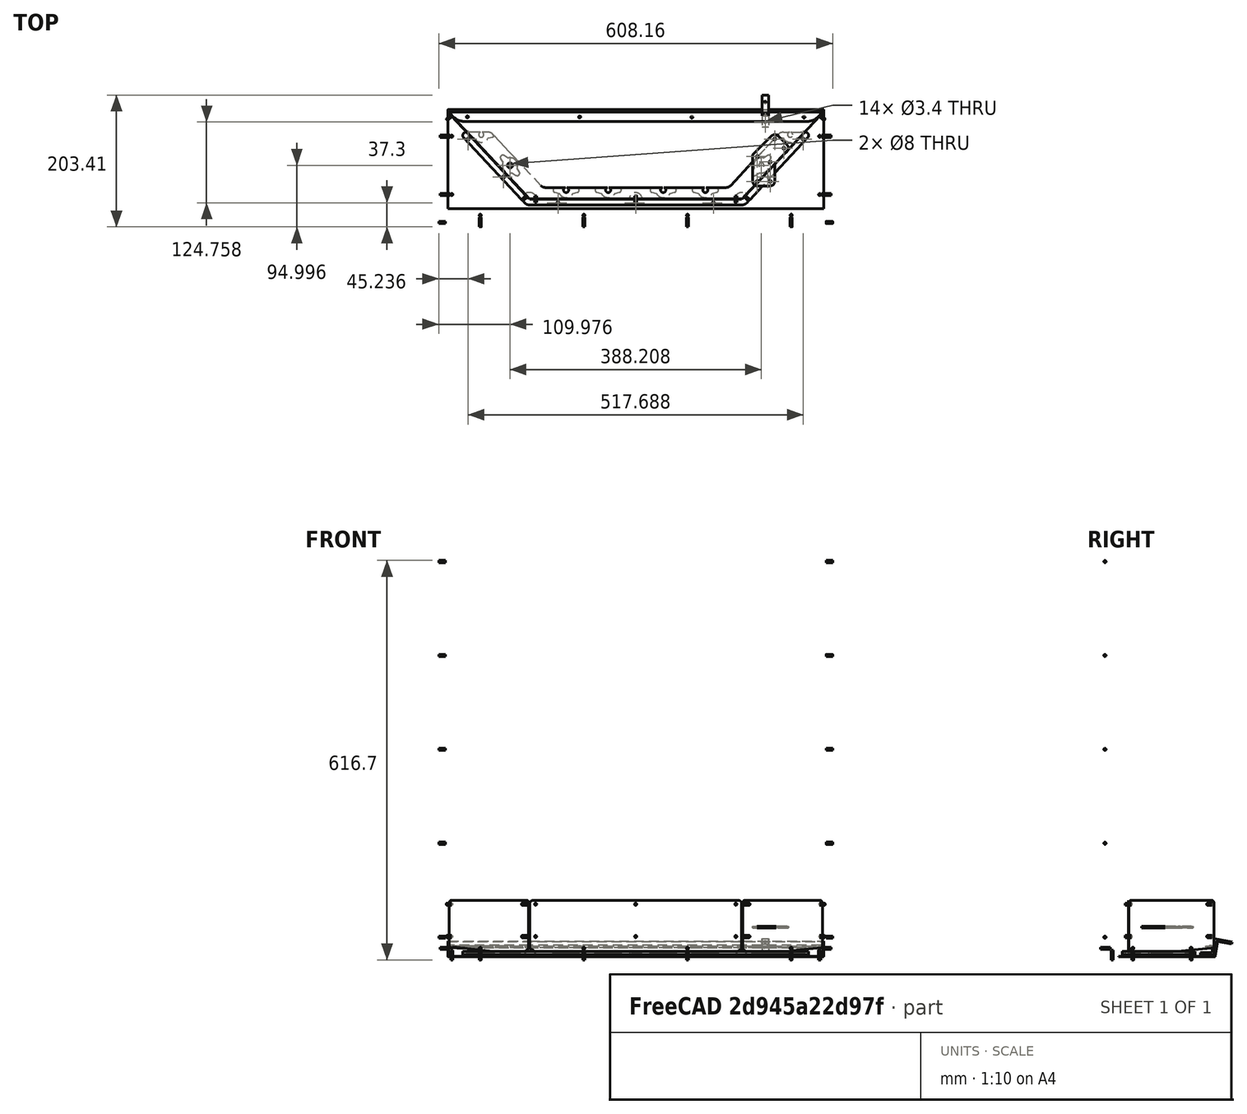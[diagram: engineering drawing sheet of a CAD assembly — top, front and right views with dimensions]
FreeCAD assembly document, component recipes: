
FREECAD ASSEMBLY — COMPONENT RECIPES ("composit_stand5")

This assembly document has 19 components, labeled P0..P18 below (a component is one placed body or linked part). 18 of them carry a construction recipe — the FreeCAD feature program that regenerates the part from scratch, quoted from this document or its linked companion documents; the rest are supplied as boundary geometry only. No exploded tour is included for this assembly.
NOTE — this tour is split across 2 documents so each fits a 32k-token context. This is document 1: the component sections continue in the remaining 1 document, each repeating the header above.
COMPONENT P0 — recipe-attached ("back_material_0.30ansi", modeled in this document).
Construction recipe (the document's own serialized feature program — sketch geometry with constraints, then the solid features built on it; lengths are millimeters unless a unit is written):

FEATURE [PartDesign::SubShapeBinder] Binder011
  BindCopyOnChange = 0
  BindMode = 0
  ClaimChildren = true
  Context = -> Body004 [Binder011.]
  Fuse = false
  MakeFace = true
  OffsetFill = false
  OffsetIntersection = false
  OffsetJoinType = 0
  OffsetOpenResult = false
  PartialLoad = false
  Relative = true
  Support = -> [Body[BaseBend.Sketch.]]
  _Version = 2
FEATURE [Sketcher::SketchObject] Sketch012
  ExternalGeometry = -> [Binder011]
  FullyConstrained = true
  MapMode = 5
  Support = -> [XY_Plane004]
  sketch-geometry (3):
    g0: LineSegment StartX=297.084 StartY=-31 StartZ=0 EndX=297.084 EndY=-41 EndZ=0
    g1: LineSegment StartX=297.084 StartY=-41 StartZ=0 EndX=-297.084 EndY=-41 EndZ=0
    g2: LineSegment StartX=-297.084 StartY=-41 StartZ=0 EndX=-297.084 EndY=-31 EndZ=0
  constraints (9):
    c: Vertical(g0)
    c: Coincident(g0,g1)
    c: Horizontal(g1)
    c: Coincident(g1,g2)
    c: Vertical(g2)
    c: Symmetric(g2,g0,g-2)
    c: DistanceY(g0,g0) = 10
    c: Horizontal(g0,g-3)
    c: DistanceX(g0,g-3) = 3
FEATURE [PartDesign::FeaturePython] BaseBend003  # WARN: FeaturePython — macro-defined, semantics opaque (R4)
  BendSide = 0
  BendSketch = -> Sketch012
  MidPlane = false
  Reverse = false
  length = 637
  radius = 0.1
  thickness = 0.3
  expr: length = BaseBend.length - 3 mm
FEATURE [PartDesign::FeaturePython] Extend  # WARN: FeaturePython — macro-defined, semantics opaque (R4)
  BaseFeature = -> BaseBend003
  Offset = 0.02
  Refine = true
  UseSubtraction = false
  baseObject = -> BaseBend003 [Face12]
  gap1 = 0
  gap2 = 0
  length = 50.4
  expr: length = <<cap_BaseBend>>.length + 0.4 mm
FEATURE [PartDesign::FeaturePython] Extend001  # WARN: FeaturePython — macro-defined, semantics opaque (R4)
  BaseFeature = -> Extend
  Offset = 0.02
  Refine = true
  UseSubtraction = false
  baseObject = -> Extend [Face12]
  gap1 = 0
  gap2 = 0
  length = 6
FEATURE [PartDesign::Boolean] Boolean002
  BaseFeature = -> Extend001
  Group = -> [Compound007]
  Type = 1
  expr: Group = <<back_cut1>>._self
FEATURE [PartDesign::Body] Body004  label="back_material_0.30ansi"
  Group = -> [Binder011,Sketch012,BaseBend003,Extend,Extend001,Boolean002]
  Origin = -> Origin004
  Tip = -> Extend001
COMPONENT P1 — recipe-attached ("Body008_material_0.30ansi", modeled in this document).
Construction recipe (the document's own serialized feature program — sketch geometry with constraints, then the solid features built on it; lengths are millimeters unless a unit is written):

FEATURE [Sketcher::SketchObject] Sketch021
  FullyConstrained = true
  MapMode = 5
  Placement = pos=(0,0,0) rot=(0.57735,0.57735,0.57735;2.0944rad)
  Support = -> [YZ_Plane009]
  sketch-geometry (5):
    g0: LineSegment StartX=27 StartY=0 StartZ=0 EndX=15 EndY=0 EndZ=0
    g1: LineSegment StartX=15 StartY=0 StartZ=0 EndX=15 EndY=16 EndZ=0
    g2: LineSegment StartX=15 StartY=16 StartZ=0 EndX=-15 EndY=16 EndZ=0
    g3: LineSegment StartX=-15 StartY=16 StartZ=0 EndX=-15 EndY=0 EndZ=0
    g4: LineSegment StartX=-15 StartY=0 StartZ=0 EndX=-27 EndY=0 EndZ=0
  constraints (15):
    c: PointOnObject(g0,g-1)
    c: PointOnObject(g0,g-1)
    c: Coincident(g0,g1)
    c: Vertical(g1)
    c: Coincident(g1,g2)
    c: PointOnObject(g3,g-1)
    c: Vertical(g3)
    c: Coincident(g3,g4)
    c: PointOnObject(g4,g-1)
    c: Symmetric(g2,g1,g-2)
    c: Coincident(g3,g2)
    c: DistanceX(g2,g2) = 30
    c: DistanceY(g1,g1) = 16  'height'
    c: Equal(g0,g4)
    c: DistanceX(g0,g0) = 12
FEATURE [PartDesign::FeaturePython] BaseBend005  # WARN: FeaturePython — macro-defined, semantics opaque (R4)
  BendSide = 0
  BendSketch = -> Sketch021
  MidPlane = true
  Reverse = false
  length = 115
  radius = 0.1
  thickness = 0.3
FEATURE [PartDesign::FeaturePython] Bend004  # WARN: FeaturePython — macro-defined, semantics opaque (R4)
  AutoMiter = true
  BaseFeature = -> BaseBend005
  BendType = 0
  LengthList = [16]
  LengthSpec = 1
  ReliefFactor = 0.7
  UseReliefFactor = false
  angle = 90
  baseObject = -> BaseBend005 [Edge45,Edge42]
  bendAList = [90]
  extend1 = 0
  extend2 = 0
  gap1 = 0
  gap2 = 0
  invert = false
  kfactor = 0.5
  length = 16
  maxExtendDist = 5
  minGap = 0.1
  minReliefGap = 1
  miterangle1 = 0
  miterangle2 = 0
  offset = 0
  radius = 0.1
  reliefType = 0
  reliefd = 1
  reliefw = 0.8
  sketchflip = false
  sketchinvert = false
  unfold = false
  expr: baseObject = tuple(BaseBend005._self; list(<<Edge45>>; <<Edge42>>))
  expr: length = Sketch021.Constraints.height
  expr: radius = BaseBend005.radius
FEATURE [Sketcher::SketchObject] Sketch022
  ExternalGeometry = -> [Sketch021]
  FullyConstrained = true
  MapMode = 5
  Support = -> [XY_Plane009]
  sketch-geometry (10):
    g0: LineSegment StartX=-35 StartY=-20.7 StartZ=0 EndX=-35 EndY=20.7 EndZ=0
    g1: LineSegment StartX=-35 StartY=20.7 StartZ=0 EndX=35 EndY=20.7 EndZ=0
    g2: LineSegment StartX=35 StartY=20.7 StartZ=0 EndX=35 EndY=-20.7 EndZ=0
    g3: LineSegment StartX=35 StartY=-20.7 StartZ=0 EndX=-35 EndY=-20.7 EndZ=0
    g4: GeomPoint X=0 Y=0 Z=0
    g5: Circle CenterX=35 CenterY=20.7 CenterZ=0 NormalX=0 NormalY=0 NormalZ=1 AngleXU=0 Radius=1.7
    g6: Circle CenterX=35 CenterY=-20.7 CenterZ=0 NormalX=0 NormalY=0 NormalZ=1 AngleXU=0 Radius=1.7
    g7: Circle CenterX=-35 CenterY=-20.7 CenterZ=0 NormalX=0 NormalY=0 NormalZ=1 AngleXU=0 Radius=1.7
    g8: Circle CenterX=-35 CenterY=20.7 CenterZ=0 NormalX=0 NormalY=0 NormalZ=1 AngleXU=0 Radius=1.7
    g9: GeomPoint X=35 Y=19 Z=0
  constraints (22):
    c: Coincident(g0,g1)
    c: Coincident(g1,g2)
    c: Coincident(g2,g3)
    c: Coincident(g3,g0)
    c: Horizontal(g1)
    c: Horizontal(g3)
    c: Vertical(g0)
    c: Vertical(g2)
    c: Symmetric(g1,g0,g4)
    c: Coincident(g4,g-1)
    c: Coincident(g6,g2)
    c: Coincident(g7,g0)
    c: Coincident(g8,g0)
    c: Coincident(g5,g1)
    c: Equal(g5,g8)
    c: Equal(g5,g7)
    c: Equal(g5,g6)
    c: Diameter(g5) = 3.4
    c: PointOnObject(g9,g2)
    c: PointOnObject(g9,g5)
    c: DistanceY(g-3,g9) = 4
    c: DistanceX(g1,g1) = 70
FEATURE [PartDesign::Pocket] Pocket016
  BaseFeature = -> Bend004
  Direction = (0,0,-1)
  Length = 5
  Length2 = 5
  Profile = -> Sketch022
  ReferenceAxis = -> Sketch022 [N_Axis]
  Reversed = true
  Type = 0
FEATURE [Sketcher::SketchObject] Sketch023
  AttachmentOffset = pos=(0,10,15) rot=(0,0,1;0rad)
  FullyConstrained = false
  MapMode = 5
  Placement = pos=(0,-15,10) rot=(1,0,0;1.5708rad)
  Support = -> [XZ_Plane009]
  sketch-geometry (8):
    g0: ArcOfCircle CenterX=47.5 CenterY=0 CenterZ=0 NormalX=0 NormalY=0 NormalZ=1 AngleXU=0 Radius=2.75 StartAngle=1.5708 EndAngle=4.71239
    g1: ArcOfCircle CenterX=86.6111 CenterY=0 CenterZ=0 NormalX=0 NormalY=0 NormalZ=1 AngleXU=0 Radius=2.75 StartAngle=4.71239 EndAngle=7.85398
    g2: LineSegment StartX=47.5 StartY=-2.75 StartZ=0 EndX=86.6111 EndY=-2.75 EndZ=0
    g3: LineSegment StartX=86.6111 StartY=2.75 StartZ=0 EndX=47.5 EndY=2.75 EndZ=0
    g4: ArcOfCircle CenterX=-47.5 CenterY=0 CenterZ=0 NormalX=0 NormalY=0 NormalZ=1 AngleXU=0 Radius=2.75 StartAngle=4.71239 EndAngle=7.85398
    g5: ArcOfCircle CenterX=-86.6111 CenterY=0 CenterZ=0 NormalX=0 NormalY=0 NormalZ=1 AngleXU=0 Radius=2.75 StartAngle=1.5708 EndAngle=4.71239
    g6: LineSegment StartX=-47.5 StartY=2.75 StartZ=0 EndX=-86.6111 EndY=2.75 EndZ=0
    g7: LineSegment StartX=-86.6111 StartY=-2.75 StartZ=0 EndX=-47.5 EndY=-2.75 EndZ=0
  constraints (17):
    c: Tangent(g0,g2) = -1.5708
    c: Tangent(g2,g1) = -1.5708
    c: Tangent(g1,g3) = -1.5708
    c: Tangent(g3,g0) = -1.5708
    c: Equal(g0,g1)
    c: PointOnObject(g0,g-1)
    c: PointOnObject(g1,g-1)
    c: Tangent(g4,g6) = -1.5708
    c: Tangent(g6,g5) = -1.5708
    c: Tangent(g5,g7) = -1.5708
    c: Tangent(g7,g4) = -1.5708
    c: Equal(g4,g5)
    c: Equal(g4,g0)
    c: Symmetric(g4,g0,g-2)
    c: Symmetric(g5,g1,g-2)
    c: Diameter(g0) = 5.5
    c: DistanceX(g4,g0) = 95
FEATURE [PartDesign::Pocket] Pocket018
  BaseFeature = -> Pocket016
  Direction = (0,1,-2e-16)
  Length = 5
  Length2 = 5
  Profile = -> Sketch023
  ReferenceAxis = -> Sketch023 [N_Axis]
  Reversed = true
  Type = 0
FEATURE [PartDesign::Body] Body008  label="Body008_material_0.30ansi"
  Group = -> [Sketch021,BaseBend005,Bend004,Sketch022,Pocket016,Sketch023,Pocket018]
  Origin = -> Origin009
  Tip = -> Pocket018
COMPONENT P2 — recipe-attached ("Body010", modeled in this document).
Construction recipe (the document's own serialized feature program — sketch geometry with constraints, then the solid features built on it; lengths are millimeters unless a unit is written):

FEATURE [PartDesign::FeatureBase] BaseFeature
  BaseFeature = -> Unfold
  Placement = pos=(0,0,0) rot=(1,0,0;1.5708rad)
  expr: Placement = .BaseFeature.Placement
FEATURE [PartDesign::SubShapeBinder] Binder020
  BindCopyOnChange = 0
  BindMode = 0
  ClaimChildren = false
  Context = -> Body010 [Binder020.]
  Fuse = false
  MakeFace = true
  OffsetFill = false
  OffsetIntersection = false
  OffsetJoinType = 0
  OffsetOpenResult = false
  PartialLoad = false
  Relative = true
  Support = -> [Unfold_Sketch_bends]
  _Version = 2
FEATURE [Sketcher::SketchObject] Sketch032
  ExternalGeometry = -> [Binder020]
  FullyConstrained = true
  MapMode = 5
  Support = -> [XY_Plane012]
  sketch-geometry (3):
    g0: Circle CenterX=154.334 CenterY=-0.975351 CenterZ=0 NormalX=0 NormalY=0 NormalZ=1 AngleXU=0 Radius=1
    g1: Circle CenterX=171.087 CenterY=6.35397 CenterZ=0 NormalX=0 NormalY=0 NormalZ=1 AngleXU=0 Radius=1
    g2: Circle CenterX=287.707 CenterY=131.643 CenterZ=0 NormalX=0 NormalY=0 NormalZ=1 AngleXU=0 Radius=1
  constraints (6):
    c: Coincident(g0,g-4)
    c: Coincident(g1,g-3)
    c: Coincident(g2,g-3)
    c: Equal(g0,g1)
    c: Equal(g0,g2)
    c: Diameter(g0) = 2
FEATURE [PartDesign::Pocket] Pocket023
  BaseFeature = -> BaseFeature
  Direction = (0,0,-1)
  Length = 5
  Length2 = 5
  Placement = pos=(0,0,0) rot=(1,0,0;1.5708rad)
  Profile = -> Sketch032
  ReferenceAxis = -> Sketch032 [N_Axis]
  Reversed = true
  Type = 0
FEATURE [PartDesign::Mirrored] Mirrored006
  BaseFeature = -> Pocket023
  MirrorPlane = -> Sketch032 [V_Axis]
  Originals = -> [Pocket023]
  Placement = pos=(0,0,0) rot=(1,0,0;1.5708rad)
FEATURE [PartDesign::Body] Body010
  BaseFeature = -> Unfold
  Group = -> [BaseFeature,Sketch032,Binder020,Pocket023,Mirrored006]
  Origin = -> Origin012
  Tip = -> Mirrored006
COMPONENT P3 — recipe-attached ("front_shield", modeled in this document).
Construction recipe (the document's own serialized feature program — sketch geometry with constraints, then the solid features built on it; lengths are millimeters unless a unit is written):

FEATURE [PartDesign::SubShapeBinder] Binder028
  BindCopyOnChange = 0
  BindMode = 0
  ClaimChildren = false
  Context = -> Body015 [Binder028.]
  Fuse = false
  MakeFace = true
  OffsetFill = false
  OffsetIntersection = false
  OffsetJoinType = 0
  OffsetOpenResult = false
  PartialLoad = false
  Relative = true
  Support = -> [Body[Sketch046.]]
  _Version = 2
FEATURE [Sketcher::SketchObject] Sketch057
  ExternalGeometry = -> [Binder028]
  FullyConstrained = true
  MapMode = 5
  Support = -> [XY_Plane018]
  sketch-geometry (2):
    g0: LineSegment StartX=281.847 StartY=125.257 StartZ=0 EndX=287.276 EndY=131.058 EndZ=0
    g1: LineSegment StartX=281.847 StartY=125.257 StartZ=0 EndX=-281.847 EndY=125.257 EndZ=0
  constraints (6):
    c: Parallel(g-3,g0)
    c: Distance(g-4,g0) = 3
    c: Coincident(g1,g0)
    c: Distance(g-4,g1) = 4.5
    c: Symmetric(g1,g1,g-2)
    c: Horizontal(g0,g-3)
FEATURE [PartDesign::FeaturePython] BaseBend009  # WARN: FeaturePython — macro-defined, semantics opaque (R4)
  BendSide = 0
  BendSketch = -> Sketch057
  MidPlane = false
  Reverse = false
  length = 115
  radius = 1
  thickness = 1
FEATURE [PartDesign::SubShapeBinder] Binder030
  BindCopyOnChange = 0
  BindMode = 0
  ClaimChildren = false
  Context = -> Body015 [Binder030.]
  Fuse = false
  MakeFace = true
  OffsetFill = false
  OffsetIntersection = false
  OffsetJoinType = 0
  OffsetOpenResult = false
  PartialLoad = false
  Relative = true
  _Version = 2
FEATURE [Sketcher::SketchObject] Sketch077
  FullyConstrained = true
  MapMode = 5
  Placement = pos=(0,0,0) rot=(1,0,0;1.5708rad)
  Support = -> [XZ_Plane018]
  sketch-geometry (1):
    g0: Circle CenterX=242 CenterY=85 CenterZ=0 NormalX=0 NormalY=0 NormalZ=1 AngleXU=0 Radius=15
  constraints (3):
    c: Diameter(g0) = 30
    c: DistanceX(g0) = 242
    c: DistanceY(g0) = 85
FEATURE [PartDesign::Pocket] Pocket052
  BaseFeature = -> BaseBend009
  Direction = (0,1,-2e-16)
  Length = 5
  Length2 = 5
  Midplane = true
  Profile = -> Sketch077
  ReferenceAxis = -> Sketch077 [N_Axis]
  Type = 1
FEATURE [Sketcher::SketchObject] Sketch078
  FullyConstrained = true
  MapMode = 5
  Placement = pos=(0,0,0) rot=(1,0,0;1.5708rad)
  Support = -> [XZ_Plane018]
  sketch-geometry (2):
    g0: Circle CenterX=271 CenterY=75 CenterZ=0 NormalX=0 NormalY=0 NormalZ=1 AngleXU=0 Radius=1.7
    g1: Circle CenterX=271 CenterY=35 CenterZ=0 NormalX=0 NormalY=0 NormalZ=1 AngleXU=0 Radius=1.7
  constraints (6):
    c: Vertical(g1,g0)
    c: DistanceY(g1,g0) = 40
    c: DistanceX(g0) = 271
    c: DistanceY(g0) = 75
    c: Equal(g1,g0)
    c: Diameter(g1) = 3.4
FEATURE [PartDesign::Pocket] Pocket
  BaseFeature = -> Pocket052
  Direction = (0,1,-2e-16)
  Length = 5
  Length2 = 5
  Midplane = true
  Profile = -> Sketch078
  ReferenceAxis = -> Sketch078 [N_Axis]
  Type = 1
FEATURE [PartDesign::Mirrored] Mirrored012
  BaseFeature = -> Pocket
  MirrorPlane = -> Sketch077 [V_Axis]
  Originals = -> [Pocket052,Pocket]
FEATURE [PartDesign::Body] Body015  label="front_shield"
  Group = -> [Sketch057,Binder028,BaseBend009,Binder030,Sketch077,Pocket052,Sketch078,Pocket,Mirrored012]
  Origin = -> Origin018
  Tip = -> Mirrored012
COMPONENT P4 — recipe-attached ("Body016_material_0.30ansi", modeled in this document).
Construction recipe (the document's own serialized feature program — sketch geometry with constraints, then the solid features built on it; lengths are millimeters unless a unit is written):

FEATURE [PartDesign::SubShapeBinder] Binder029
  BindCopyOnChange = 0
  BindMode = 0
  ClaimChildren = false
  Context = -> Body016 [Binder029.]
  Fuse = false
  MakeFace = true
  OffsetFill = false
  OffsetIntersection = false
  OffsetJoinType = 0
  OffsetOpenResult = false
  PartialLoad = false
  Relative = true
  Support = -> [Body[BaseBend.Sketch.]]
  _Version = 2
FEATURE [Sketcher::SketchObject] Sketch058
  ExternalGeometry = -> [Binder029]
  FullyConstrained = true
  MapMode = 5
  Support = -> [XY_Plane019]
  sketch-geometry (9):
    g0: LineSegment StartX=-297.084 StartY=131.058 StartZ=0 EndX=-297.084 EndY=-38 EndZ=0
    g1: LineSegment StartX=-297.084 StartY=-38 StartZ=0 EndX=297.084 EndY=-38 EndZ=0
    g2: LineSegment StartX=297.084 StartY=-38 StartZ=0 EndX=297.084 EndY=131.058 EndZ=0
    g3: LineSegment StartX=297.084 StartY=131.058 StartZ=0 EndX=-297.084 EndY=131.058 EndZ=0
    g4: GeomPoint X=0 Y=46.5289 Z=0
    g5: LineSegment StartX=297.084 StartY=134.058 StartZ=0 EndX=297.084 EndY=131.058 EndZ=0
    g6: LineSegment StartX=297.084 StartY=131.058 StartZ=0 EndX=300.084 EndY=131.058 EndZ=0
    g7: LineSegment StartX=297.084 StartY=-41 StartZ=0 EndX=297.084 EndY=-38 EndZ=0
    g8: LineSegment StartX=297.084 StartY=-38 StartZ=0 EndX=300.084 EndY=-38 EndZ=0
  constraints (25):
    c: Coincident(g0,g1)
    c: Coincident(g1,g2)
    c: Coincident(g2,g3)
    c: Coincident(g3,g0)
    c: Horizontal(g1)
    c: Horizontal(g3)
    c: Vertical(g0)
    c: Vertical(g2)
    c: Symmetric(g1,g0,g4)
    c: PointOnObject(g4,g-2)
    c: Coincident(g5,g2)
    c: Coincident(g5,g6)
    c: PointOnObject(g6,g-3)
    c: Coincident(g7,g1)
    c: Coincident(g7,g8)
    c: PointOnObject(g8,g-3)
    c: Horizontal(g8)
    c: Horizontal(g7,g-3)
    c: Vertical(g7)
    c: Equal(g7,g8)
    c: Equal(g8,g6)
    c: Equal(g6,g5)
    c: Horizontal(g5,g-3)
    c: Parallel(g5,g2)
    c: DistanceX(g6,g6) = 3
FEATURE [PartDesign::FeaturePython] BaseBend010  # WARN: FeaturePython — macro-defined, semantics opaque (R4)
  BendSide = 0
  BendSketch = -> Sketch058
  MidPlane = false
  Reverse = true
  length = 100
  radius = 0.1
  thickness = 0.3
  expr: radius = composit_properties#<<Properties>>.bend_r
  expr: thickness = composit_properties#<<Properties>>.al_thickness
FEATURE [PartDesign::FeaturePython] Bend009  # WARN: FeaturePython — macro-defined, semantics opaque (R4)
  AutoMiter = true
  BaseFeature = -> BaseBend010
  BendType = 1
  LengthList = [3]
  LengthSpec = 1
  ReliefFactor = 0.7
  UseReliefFactor = false
  angle = 90
  baseObject = -> BaseBend010 [Edge11]
  bendAList = [90]
  extend1 = 0
  extend2 = 0
  gap1 = 0
  gap2 = 0
  invert = false
  kfactor = 0.5
  length = 3
  maxExtendDist = 5
  minGap = 0.1
  minReliefGap = 1
  miterangle1 = 0
  miterangle2 = 0
  offset = 0
  radius = 0.1
  reliefType = 0
  reliefd = 1
  reliefw = 0.8
  sketchflip = false
  sketchinvert = false
  unfold = false
  expr: length = composit_properties#<<Properties>>.thickness
  expr: radius = BaseBend005.radius
FEATURE [Sketcher::SketchObject] Sketch059
  ExternalGeometry = -> [Sketch058]
  FullyConstrained = true
  MapMode = 5
  Support = -> [XY_Plane019]
  sketch-geometry (7):
    g0: LineSegment StartX=0 StartY=131.058 StartZ=0 EndX=0 EndY=121.058 EndZ=0
    g1: LineSegment StartX=0 StartY=-28 StartZ=0 EndX=0 EndY=-38 EndZ=0
    g2: Circle CenterX=0 CenterY=121.058 CenterZ=0 NormalX=0 NormalY=0 NormalZ=1 AngleXU=0 Radius=1.7
    g3: Circle CenterX=0 CenterY=-28 CenterZ=0 NormalX=0 NormalY=0 NormalZ=1 AngleXU=0 Radius=1.7
    g4: LineSegment StartX=0 StartY=121.058 StartZ=0 EndX=0 EndY=46.5289 EndZ=0
    g5: LineSegment StartX=0 StartY=46.5289 StartZ=0 EndX=0 EndY=-28 EndZ=0
    g6: Circle CenterX=0 CenterY=46.5289 CenterZ=0 NormalX=0 NormalY=0 NormalZ=1 AngleXU=0 Radius=1.7
  constraints (19):
    c: PointOnObject(g0,g-3)
    c: PointOnObject(g0,g-2)
    c: Vertical(g0)
    c: Coincident(g0,g4)
    c: PointOnObject(g5,g-2)
    c: Coincident(g5,g1)
    c: PointOnObject(g1,g-4)
    c: Vertical(g1)
    c: Coincident(g2,g0)
    c: Coincident(g3,g5)
    c: Coincident(g4,g5)
    c: Coincident(g6,g4)
    c: Equal(g5,g4)
    c: Equal(g0,g1)
    c: DistanceY(g1,g1) = 10
    c: Equal(g3,g6)
    c: Equal(g3,g2)
    c: Diameter(g3) = 3.4
    c: PointOnObject(g6,g-2)
FEATURE [PartDesign::Boolean] Boolean003
  BaseFeature = -> Bend009
  Type = 1
FEATURE [PartDesign::Body] Body016  label="Body016_material_0.30ansi"
  Group = -> [Binder029,Sketch058,BaseBend010,Bend009,Sketch059,Boolean003]
  Origin = -> Origin019
  Placement = pos=(0,0,-3) rot=(0,0,1;0rad)
  Tip = -> Boolean003
COMPONENT P5 — recipe-attached ("Body019", modeled in this document).
Construction recipe (the document's own serialized feature program — sketch geometry with constraints, then the solid features built on it; lengths are millimeters unless a unit is written):

FEATURE [PartDesign::SubShapeBinder] Binder033
  BindCopyOnChange = 0
  BindMode = 0
  ClaimChildren = false
  Context = -> Body019 [Binder033.]
  Fuse = false
  MakeFace = true
  OffsetFill = false
  OffsetIntersection = false
  OffsetJoinType = 0
  OffsetOpenResult = false
  PartialLoad = false
  Relative = true
  Support = -> [Sketch005]
  _Version = 2
FEATURE [Sketcher::SketchObject] Sketch062
  ExternalGeometry = -> [Binder033]
  FullyConstrained = true
  MapMode = 5
  Support = -> [XY_Plane022]
  sketch-geometry (9):
    g0: LineSegment StartX=280.724 StartY=124.058 StartZ=0 EndX=261.224 EndY=124.058 EndZ=0
    g1: LineSegment StartX=261.224 StartY=124.058 StartZ=0 EndX=261.224 EndY=103.223 EndZ=0
    g2: LineSegment StartX=261.224 StartY=103.223 StartZ=0 EndX=280.724 EndY=124.058 EndZ=0
    g3: LineSegment StartX=273.808 StartY=121.058 StartZ=0 EndX=264.224 EndY=121.058 EndZ=0
    g4: LineSegment StartX=264.224 StartY=121.058 StartZ=0 EndX=264.224 EndY=110.819 EndZ=0
    g5: LineSegment StartX=264.224 StartY=110.819 StartZ=0 EndX=273.808 EndY=121.058 EndZ=0
    g6: LineSegment StartX=273.808 StartY=124.058 StartZ=0 EndX=273.808 EndY=121.058 EndZ=0
    g7: LineSegment StartX=273.808 StartY=121.058 StartZ=0 EndX=275.998 EndY=119.008 EndZ=0
    g8: LineSegment StartX=264.224 StartY=110.819 StartZ=0 EndX=261.224 EndY=110.819 EndZ=0
  constraints (27):
    c: PointOnObject(g0,g-3)
    c: Horizontal(g0)
    c: Coincident(g0,g1)
    c: PointOnObject(g1,g-3)
    c: Vertical(g1)
    c: Coincident(g1,g2)
    c: Coincident(g2,g0)
    c: DistanceX(g0,g0) = 19.5
    c: DistanceY(g0,g-3) = 10
    c: Coincident(g3,g4)
    c: Coincident(g4,g5)
    c: Coincident(g5,g3)
    c: Parallel(g3,g0)
    c: Parallel(g4,g1)
    c: Parallel(g5,g2)
    c: PointOnObject(g6,g0)
    c: Coincident(g6,g3)
    c: Coincident(g6,g7)
    c: PointOnObject(g7,g2)
    c: Coincident(g4,g8)
    c: PointOnObject(g8,g1)
    c: Horizontal(g8)
    c: Vertical(g6)
    c: Perpendicular(g2,g7)
    c: Equal(g7,g6)
    c: Equal(g6,g8)
    c: DistanceX(g8,g8) = 3
FEATURE [PartDesign::Pad] Pad007
  Direction = (0,0,1)
  Length = 18
  Length2 = 10
  Profile = -> Sketch062
  ReferenceAxis = -> Sketch062 [N_Axis]
  Type = 0
FEATURE [Sketcher::SketchObject] Sketch063
  AttachmentOffset = pos=(0,0,-124.1) rot=(0,0,1;0rad)
  ExternalGeometry = -> [Sketch062]
  FullyConstrained = true
  MapMode = 5
  Placement = pos=(0,124.1,-2.76e-14) rot=(1,0,0;1.5708rad)
  Support = -> [XZ_Plane022]
  expr: Constraints[5] = Pad007.Length / 2
  sketch-geometry (3):
    g0: Circle CenterX=270.974 CenterY=9 CenterZ=0 NormalX=0 NormalY=0 NormalZ=1 AngleXU=0 Radius=1.7
    g1: LineSegment StartX=280.724 StartY=-2.75e-14 StartZ=0 EndX=270.974 EndY=9 EndZ=0
    g2: LineSegment StartX=270.974 StartY=9 StartZ=0 EndX=261.224 EndY=-2.84e-14 EndZ=0
  constraints (7):
    c: Coincident(g-3,g1)
    c: Coincident(g1,g0)
    c: Coincident(g1,g2)
    c: Coincident(g2,g-3)
    c: Equal(g2,g1)
    c: DistanceY(g-3,g0) = 9
    c: Diameter(g0) = 3.4
FEATURE [PartDesign::Hole] Hole002
  BaseFeature = -> Pad007
  CustomThreadClearance = 0
  Depth = 8
  DepthType = 0
  Diameter = 3.4
  DrillForDepth = false
  DrillPoint = 1
  DrillPointAngle = 118
  HoleCutCountersinkAngle = 90
  HoleCutCustomValues = false
  HoleCutDepth = 0
  HoleCutDiameter = 6.1
  HoleCutType = 0
  ModelThread = false
  Profile = -> Sketch063
  Reversed = true
  Tapered = false
  TaperedAngle = 90
  ThreadClass = 0
  ThreadDepth = 8
  ThreadDepthType = 0
  ThreadDirection = 0
  ThreadFit = 0
  ThreadSize = 0
  ThreadType = 0
  Threaded = false
  UseCustomThreadClearance = false
FEATURE [Sketcher::SketchObject] Sketch064
  AttachmentOffset = pos=(0,0,0) rot=(0,1,0;1.5708rad)
  FullyConstrained = true
  MapMode = 7
  Placement = pos=(271.619,114.329,0) rot=(0.852419,0.369717,0.369717;1.7298rad)
  Support = -> [Sketch062]
  sketch-geometry (2):
    g0: Circle CenterX=0.6273 CenterY=4 CenterZ=0 NormalX=0 NormalY=0 NormalZ=1 AngleXU=0 Radius=1.7
    g1: Circle CenterX=0.6273 CenterY=14 CenterZ=0 NormalX=0 NormalY=0 NormalZ=1 AngleXU=0 Radius=1.7
  constraints (6):
    c: Diameter(g0) = 3.4
    c: DistanceY(g0) = 4
    c: DistanceX(g0) = 0.6273
    c: Equal(g1,g0)
    c: Vertical(g1,g0)
    c: DistanceY(g0,g1) = 10
FEATURE [Sketcher::SketchObject] Sketch065
  ExternalGeometry = -> [Sketch062]
  FullyConstrained = true
  MapMode = 5
  Support = -> [XY_Plane022]
  sketch-geometry (4):
    g0: LineSegment StartX=261.224 StartY=106.15 StartZ=0 EndX=275.574 EndY=121.482 EndZ=0
    g1: LineSegment StartX=261.224 StartY=124.058 StartZ=0 EndX=261.224 EndY=106.15 EndZ=0
    g2: LineSegment StartX=275.574 StartY=121.482 StartZ=0 EndX=272.822 EndY=124.058 EndZ=0
    g3: LineSegment StartX=272.822 StartY=124.058 StartZ=0 EndX=261.224 EndY=124.058 EndZ=0
  constraints (12):
    c: Coincident(g0,g2)
    c: Coincident(g3,g1)
    c: Coincident(g1,g0)
    c: Vertical(g1)
    c: Vertical(g0,g-3)
    c: Parallel(g0,g-3)
    c: Distance(g0) = 21
    c: Coincident(g2,g3)
    c: Perpendicular(g0,g2)
    c: Horizontal(g2,g-3)
    c: Distance(g0,g-3) = 2
    c: Horizontal(g3)
FEATURE [PartDesign::Plane] DatumPlane001
  AttachmentOffset = pos=(0,0,9) rot=(0,0,1;0rad)
  Length = 348.425
  MapMode = 5
  Placement = pos=(0,0,9) rot=(0,0,1;0rad)
  ResizeMode = 0
  Support = -> [XY_Plane022]
  Width = 191.801
  expr: .AttachmentOffset.Base.z = Pad007.Length / 2
FEATURE [Sketcher::SketchObject] Sketch066
  AttachmentOffset = pos=(0,0,-2) rot=(0,0,1;0rad)
  ExternalGeometry = -> [Sketch064]
  FullyConstrained = true
  MapMode = 2
  Placement = pos=(270.159,115.696,3e-16) rot=(0.852419,0.369717,0.369717;1.7298rad)
  Support = -> [Sketch064]
  sketch-geometry (1):
    g0: Circle CenterX=0.6273 CenterY=4 CenterZ=0 NormalX=0 NormalY=0 NormalZ=1 AngleXU=0 Radius=4
  constraints (2):
    c: Coincident(g0,g-3)
    c: Diameter(g0) = 8
FEATURE [Sketcher::SketchObject] Sketch071
  ExternalGeometry = -> [Sketch063]
  FullyConstrained = true
  MapMode = 2
  Placement = pos=(0,124.1,-2.76e-14) rot=(1,0,0;1.5708rad)
  Support = -> [Sketch063]
  sketch-geometry (1):
    g0: Circle CenterX=270.974 CenterY=9 CenterZ=0 NormalX=0 NormalY=0 NormalZ=1 AngleXU=0 Radius=9
  constraints (2):
    c: Coincident(g0,g-3)
    c: Diameter(g0) = 18
FEATURE [Part::FeaturePython] WireFilter  # WARN: FeaturePython — macro-defined, semantics opaque (R4)
  AttacherType = Attacher::AttachEngine3D
  ClaimChildren = true
  ColorKeyCount = 8
  Colorize = true
  FaceMaker = 5
  FixNormal = false
  FollowSource = true
  InvertedFaceScale = 5
  MaxWires = 25
  Normal = (0,1,2e-16)
  OffsetFill = false
  OffsetIntersection = false
  OffsetJoin = 0
  OffsetOpenResult = false
  Scale = (1,1,1)
  SelectEdges = false
  Source = -> Sketch071
  UniformScale = 1
  UseDefault = false
  UseSelected = true
  UseSelectedEdges = false
  Version = 0.2022.02.09
  WireOrder = [1]
FEATURE [Sketcher::SketchObject] Sketch072
  AttachmentOffset = pos=(0,0,2) rot=(0,0,1;0rad)
  ExternalGeometry = -> [Sketch063]
  FullyConstrained = true
  MapMode = 2
  Placement = pos=(0,122.1,-2.71e-14) rot=(1,0,0;1.5708rad)
  Support = -> [Sketch063]
  sketch-geometry (1):
    g0: Circle CenterX=270.974 CenterY=9 CenterZ=0 NormalX=0 NormalY=0 NormalZ=1 AngleXU=0 Radius=2.5
  constraints (2):
    c: Coincident(g0,g-3)
    c: Diameter(g0) = 5
FEATURE [PartDesign::Pocket] Pocket045
  BaseFeature = -> Hole002
  Direction = (0,1,-2e-16)
  Length = 5
  Length2 = 5
  Profile = -> Sketch072
  ReferenceAxis = -> Sketch072 [N_Axis]
  Reversed = true
  Type = 0
FEATURE [Sketcher::SketchObject] Sketch073
  FullyConstrained = false
  MapMode = 2
  Placement = pos=(271.619,114.329,0) rot=(0.852419,0.369717,0.369717;1.7298rad)
  Support = -> [Sketch064]
  sketch-geometry (4):
    g0: LineSegment StartX=-6 StartY=0 StartZ=0 EndX=-24.5767 EndY=0 EndZ=0
    g1: LineSegment StartX=-24.5767 StartY=0 StartZ=0 EndX=-24.5767 EndY=27.1269 EndZ=0
    g2: LineSegment StartX=-24.5767 StartY=27.1269 StartZ=0 EndX=-6 EndY=27.1269 EndZ=0
    g3: LineSegment StartX=-6 StartY=27.1269 StartZ=0 EndX=-6 EndY=0 EndZ=0
  constraints (10):
    c: Coincident(g0,g1)
    c: Coincident(g1,g2)
    c: Coincident(g2,g3)
    c: Coincident(g3,g0)
    c: Horizontal(g0)
    c: Horizontal(g2)
    c: Vertical(g1)
    c: Vertical(g3)
    c: PointOnObject(g0,g-1)
    c: DistanceX(g0) = -6
FEATURE [PartDesign::Pocket] Pocket046
  BaseFeature = -> Pocket045
  Direction = (-0.730107,0.683333,2e-16)
  Length = 5
  Length2 = 5
  Midplane = true
  Profile = -> Sketch073
  ReferenceAxis = -> Sketch073 [N_Axis]
  Type = 1
FEATURE [PartDesign::Pocket] Pocket040
  BaseFeature = -> Pocket046
  Direction = (-0.730107,0.683333,0)
  Length = 5
  Length2 = 5
  Midplane = true
  Profile = -> Sketch064
  ReferenceAxis = -> Sketch064 [N_Axis]
  Type = 1
FEATURE [PartDesign::Pocket] Pocket041
  BaseFeature = -> Pocket040
  Direction = (-0.730107,0.683333,2e-16)
  Length = 5
  Length2 = 5
  Profile = -> Sketch066
  ReferenceAxis = -> Sketch066 [N_Axis]
  Type = 1
FEATURE [PartDesign::Mirrored] Mirrored010
  BaseFeature = -> Pocket041
  MirrorPlane = -> DatumPlane001
  Originals = -> [Pocket040,Pocket041]
FEATURE [PartDesign::Pocket] Pocket044
  BaseFeature = -> Mirrored010
  Direction = (0,-1,-2e-16)
  Length = 5
  Length2 = 5
  Profile = -> WireFilter
  Type = 1
FEATURE [PartDesign::Body] Body019
  Group = -> [Binder033,Sketch062,Pad007,Sketch063,Hole002,Sketch064,Sketch065,DatumPlane001,Sketch071,Sketch072,Pocket045,Sketch073,Pocket046,Pocket040,Pocket041,Mirrored010,Sketch066,WireFilter,Pocket044]
  Origin = -> Origin022
  Placement = pos=(0,0,50) rot=(0,0,1;0rad)
  Tip = -> Pocket044
COMPONENT P6 — recipe-attached ("electric_shield", modeled in this document).
Construction recipe (the document's own serialized feature program — sketch geometry with constraints, then the solid features built on it; lengths are millimeters unless a unit is written):

FEATURE [PartDesign::SubShapeBinder] Binder035
  BindCopyOnChange = 0
  BindMode = 0
  ClaimChildren = false
  Context = -> Body020 [Binder035.]
  Fuse = false
  MakeFace = true
  OffsetFill = false
  OffsetIntersection = false
  OffsetJoinType = 0
  OffsetOpenResult = false
  PartialLoad = false
  Relative = true
  Support = -> [Compound009]
  _Version = 2
FEATURE [PartDesign::Pad] Pad008  label="electric_shield_extrude"
  Direction = (0,0,1)
  Length = 3
  Length2 = 10
  Profile = -> Binder035
  Type = 0
FEATURE [PartDesign::Boolean] Boolean007
  BaseFeature = -> Pad008
  Type = 1
FEATURE [PartDesign::Body] Body020  label="electric_shield"
  Group = -> [Binder035,Pad008,Boolean007]
  Origin = -> Origin023
  Tip = -> Boolean007
COMPONENT P7 — recipe-attached ("Body021", modeled in this document).
Construction recipe (the document's own serialized feature program — sketch geometry with constraints, then the solid features built on it; lengths are millimeters unless a unit is written):

FEATURE [PartDesign::SubShapeBinder] Binder038
  BindCopyOnChange = 0
  BindMode = 0
  ClaimChildren = false
  Context = -> Body021 [Binder038.]
  Fuse = false
  MakeFace = true
  OffsetFill = false
  OffsetIntersection = false
  OffsetJoinType = 0
  OffsetOpenResult = false
  PartialLoad = false
  Relative = true
  Support = -> [Body016[BaseBend010.Sketch058.]]
  _Version = 2
FEATURE [PartDesign::Pad] Pad009
  Direction = (0,0,1)
  Length = 3
  Length2 = 10
  Profile = -> Binder038
  Type = 0
FEATURE [PartDesign::Boolean] Boolean004
  BaseFeature = -> Pad009
  Type = 1
FEATURE [Sketcher::SketchObject] Sketch075
  ExternalGeometry = -> [Binder038]
  FullyConstrained = true
  MapMode = 5
  Placement = pos=(0,0,0) rot=(0.57735,0.57735,0.57735;2.0944rad)
  Support = -> [YZ_Plane024]
  sketch-geometry (3):
    g0: LineSegment StartX=131.058 StartY=3 StartZ=0 EndX=129.558 EndY=3 EndZ=0
    g1: LineSegment StartX=129.558 StartY=3 StartZ=0 EndX=131.058 EndY=1.5 EndZ=0
    g2: LineSegment StartX=131.058 StartY=1.5 StartZ=0 EndX=131.058 EndY=3 EndZ=0
  constraints (9):
    c: Horizontal(g0)
    c: Coincident(g0,g1)
    c: Coincident(g1,g2)
    c: Coincident(g2,g0)
    c: Vertical(g2)
    c: Equal(g2,g0)
    c: DistanceX(g0,g0) = 1.5
    c: DistanceY(g-3,g0) = 3
    c: Vertical(g0,g-3)
FEATURE [PartDesign::Pocket] Pocket049
  BaseFeature = -> Boolean004
  Direction = (-1,0,0)
  Length = 540
  Length2 = 5
  Midplane = true
  Profile = -> Sketch075
  ReferenceAxis = -> Sketch075 [N_Axis]
  Type = 0
FEATURE [PartDesign::Body] Body021
  Group = -> [Binder038,Pad009,Boolean004,Sketch075,Pocket049]
  Origin = -> Origin024
  Placement = pos=(0,0,-3) rot=(0,0,1;0rad)
  Tip = -> Pocket049
COMPONENT P8 — recipe-attached ("electric_shield_jamb", modeled in this document).
Construction recipe (the document's own serialized feature program — sketch geometry with constraints, then the solid features built on it; lengths are millimeters unless a unit is written):

FEATURE [PartDesign::SubShapeBinder] Binder043
  BindCopyOnChange = 0
  BindMode = 0
  ClaimChildren = true
  Context = -> Body023 [Binder043.]
  Fuse = false
  MakeFace = true
  OffsetFill = false
  OffsetIntersection = false
  OffsetJoinType = 0
  OffsetOpenResult = false
  PartialLoad = false
  Relative = false
  Support = -> [Sketch068]
  _Version = 2
FEATURE [PartDesign::Pad] Pad011
  Direction = (0,0,1)
  Length = 3
  Length2 = 10
  Profile = -> Binder043
  Type = 0
FEATURE [PartDesign::Boolean] Boolean008
  BaseFeature = -> Pad011
  Refine = true
  Type = 1
FEATURE [PartDesign::Body] Body023  label="electric_shield_jamb"
  Group = -> [Binder043,Pad011,Boolean008]
  Origin = -> Origin026
  Tip = -> Boolean008
COMPONENT P9 — recipe-attached ("Body024", modeled in this document).
Construction recipe (the document's own serialized feature program — sketch geometry with constraints, then the solid features built on it; lengths are millimeters unless a unit is written):

FEATURE [PartDesign::SubShapeBinder] Binder046
  BindCopyOnChange = 0
  BindMode = 0
  ClaimChildren = false
  Context = -> Body024 [Binder046.]
  Fuse = false
  MakeFace = true
  OffsetFill = false
  OffsetIntersection = false
  OffsetJoinType = 0
  OffsetOpenResult = false
  PartialLoad = false
  Relative = true
  Support = -> [Sketch005]
  _Version = 2
FEATURE [Sketcher::SketchObject] Sketch091
  ExternalGeometry = -> [Binder046]
  FullyConstrained = true
  MapMode = 5
  Support = -> [XY_Plane027]
  sketch-geometry (5):
    g0: LineSegment StartX=257.917 StartY=124.058 StartZ=0 EndX=277.917 EndY=124.058 EndZ=0
    g1: LineSegment StartX=277.917 StartY=124.058 StartZ=0 EndX=277.917 EndY=121.058 EndZ=0
    g2: LineSegment StartX=277.917 StartY=121.058 StartZ=0 EndX=268.578 EndY=111.08 EndZ=0
    g3: LineSegment StartX=268.578 StartY=111.08 StartZ=0 EndX=257.917 EndY=121.058 EndZ=0
    g4: LineSegment StartX=257.917 StartY=121.058 StartZ=0 EndX=257.917 EndY=124.058 EndZ=0
  constraints (16):
    c: Horizontal(g0)
    c: Coincident(g0,g1)
    c: PointOnObject(g1,g-3)
    c: Vertical(g1)
    c: Coincident(g1,g2)
    c: PointOnObject(g2,g-3)
    c: Coincident(g2,g3)
    c: Coincident(g4,g0)
    c: DistanceX(g0,g0) = 20
    c: DistanceY(g1,g1) = 3
    c: DistanceY(g0,g-3) = 10
    c: Coincident(g3,g4)
    c: Vertical(g4)
    c: Perpendicular(g2,g3)
    c: Horizontal(g3,g1)
    c: DistanceY(g0) = 124.058  'face_offset'
FEATURE [PartDesign::Pad] Pad019
  Direction = (0,0,1)
  Length = 105
  Length2 = 10
  Profile = -> Sketch091
  ReferenceAxis = -> Sketch091 [N_Axis]
  Type = 0
FEATURE [Sketcher::SketchObject] Sketch092
  AttachmentOffset = pos=(0,0,-124.058) rot=(0,0,1;0rad)
  ExternalGeometry = -> [Sketch091]
  FullyConstrained = true
  MapMode = 5
  Placement = pos=(0,124.058,-2.75e-14) rot=(1,0,0;1.5708rad)
  Support = -> [XZ_Plane027]
  expr: .AttachmentOffset.Base.z = -Sketch091.Constraints.face_offset
  sketch-geometry (3):
    g0: Circle CenterX=267.917 CenterY=52.5 CenterZ=0 NormalX=0 NormalY=0 NormalZ=1 AngleXU=0 Radius=9.95
    g1: LineSegment StartX=257.917 StartY=-2.75e-14 StartZ=0 EndX=267.917 EndY=52.5 EndZ=0
    g2: LineSegment StartX=267.917 StartY=52.5 StartZ=0 EndX=277.917 EndY=-2.84e-14 EndZ=0
  constraints (7):
    c: Diameter(g0) = 19.9
    c: Coincident(g-3,g1)
    c: Coincident(g1,g0)
    c: Coincident(g1,g2)
    c: Coincident(g2,g-3)
    c: Equal(g2,g1)
    c: DistanceY(g0) = 52.5
FEATURE [PartDesign::Pocket] Pocket062
  BaseFeature = -> Pad019
  Direction = (0,1,-2e-16)
  Length = 3
  Length2 = 5
  Profile = -> Sketch092
  ReferenceAxis = -> Sketch092 [N_Axis]
  Reversed = true
  Type = 0
FEATURE [Sketcher::SketchObject] Sketch093
  ExternalGeometry = -> [Sketch092]
  FullyConstrained = true
  MapMode = 5
  Placement = pos=(0,0,0) rot=(1,0,0;1.5708rad)
  Support = -> [XZ_Plane027]
  sketch-geometry (7):
    g0: LineSegment StartX=271.381 StartY=52.5 StartZ=0 EndX=269.649 EndY=55.5 EndZ=0
    g1: LineSegment StartX=269.649 StartY=55.5 StartZ=0 EndX=266.185 EndY=55.5 EndZ=0
    g2: LineSegment StartX=266.185 StartY=55.5 StartZ=0 EndX=264.453 EndY=52.5 EndZ=0
    g3: LineSegment StartX=264.453 StartY=52.5 StartZ=0 EndX=266.185 EndY=49.5 EndZ=0
    g4: LineSegment StartX=266.185 StartY=49.5 StartZ=0 EndX=269.649 EndY=49.5 EndZ=0
    g5: LineSegment StartX=269.649 StartY=49.5 StartZ=0 EndX=271.381 EndY=52.5 EndZ=0
    g6: Circle CenterX=267.917 CenterY=52.5 CenterZ=0 NormalX=0 NormalY=0 NormalZ=1 AngleXU=0 Radius=3.4641
  constraints (16):
    c: Coincident(g0,g1)
    c: Coincident(g1,g2)
    c: Coincident(g2,g3)
    c: Coincident(g3,g4)
    c: Coincident(g4,g5)
    c: Coincident(g5,g0)
    c: Equal(g0, g1-g5) x5
    c: PointOnObject(g0,g6)
    c: PointOnObject(g1,g6)
    c: PointOnObject(g2,g6)
    c: PointOnObject(g3,g6)
    c: PointOnObject(g4,g6)
    c: PointOnObject(g5,g6)
    c: Coincident(g6,g-3)
    c: Horizontal(g1)
    c: DistanceY(g4,g0) = 6
FEATURE [PartDesign::Pocket] Pocket063
  BaseFeature = -> Pocket062
  Direction = (0,1,-2e-16)
  Length = 119.058
  Length2 = 5
  Profile = -> Sketch093
  ReferenceAxis = -> Sketch093 [N_Axis]
  Type = 0
  expr: Length = Sketch091.Constraints.face_offset - 5 mm
FEATURE [PartDesign::Hole] Hole
  BaseFeature = -> Pocket063
  CustomThreadClearance = 0
  Depth = 217.499
  DepthType = 1
  Diameter = 3.5
  DrillForDepth = false
  DrillPoint = 1
  DrillPointAngle = 118
  HoleCutCountersinkAngle = 90
  HoleCutCustomValues = false
  HoleCutDepth = 0
  HoleCutDiameter = 6.1
  HoleCutType = 0
  ModelThread = false
  Profile = -> Sketch092
  Reversed = true
  Tapered = false
  TaperedAngle = 90
  ThreadClass = 0
  ThreadDepth = 217.499
  ThreadDepthType = 0
  ThreadDirection = 0
  ThreadFit = 0
  ThreadSize = 0
  ThreadType = 0
  Threaded = false
  UseCustomThreadClearance = false
FEATURE [Sketcher::SketchObject] Sketch094
  AttachmentOffset = pos=(0,0,0) rot=(0,1,0;1.5708rad)
  ExternalGeometry = -> [Sketch091]
  FullyConstrained = true
  MapMode = 7
  Placement = pos=(277.917,121.058,0) rot=(-0.293211,0.676028,0.676028;3.71203rad)
  Support = -> [Sketch091]
  sketch-geometry (1):
    g0: Circle CenterX=8.66667 CenterY=10 CenterZ=0 NormalX=0 NormalY=0 NormalZ=1 AngleXU=0 Radius=1.7
  constraints (3):
    c: Diameter(g0) = 3.4
    c: DistanceX(g0,g-3) = 5
    c: DistanceY(g0) = 10
FEATURE [PartDesign::Hole] Hole003
  BaseFeature = -> Hole
  CustomThreadClearance = 0
  Depth = 217.499
  DepthType = 1
  Diameter = 3.4
  DrillForDepth = false
  DrillPoint = 1
  DrillPointAngle = 118
  HoleCutCountersinkAngle = 90
  HoleCutCustomValues = false
  HoleCutDepth = 0
  HoleCutDiameter = 6.1
  HoleCutType = 0
  ModelThread = false
  Profile = -> Sketch094
  Reversed = true
  Tapered = false
  TaperedAngle = 90
  ThreadClass = 0
  ThreadDepth = 217.499
  ThreadDepthType = 0
  ThreadDirection = 0
  ThreadFit = 0
  ThreadSize = 0
  ThreadType = 0
  Threaded = false
  UseCustomThreadClearance = false
FEATURE [PartDesign::SubShapeBinder] Binder047
  BindCopyOnChange = 0
  BindMode = 0
  ClaimChildren = false
  Context = -> Body024 [Binder047.]
  Fuse = false
  MakeFace = true
  OffsetFill = false
  OffsetIntersection = false
  OffsetJoinType = 0
  OffsetOpenResult = false
  PartialLoad = false
  Placement = pos=(276.456,122.425,0) rot=(-0.293211,0.676028,0.676028;3.71203rad)
  Relative = false
  Support = -> [Hole003[Sketch094.]]
  _Version = 2
  expr: Placement = Sketch094.Placement * placement(vector(0; 0; 2); rotation(0; 0; 0))
FEATURE [PartDesign::Hole] Hole004
  BaseFeature = -> Hole003
  CustomThreadClearance = 0
  Depth = 25
  DepthType = 0
  Diameter = 10
  DrillForDepth = false
  DrillPoint = 1
  DrillPointAngle = 118
  HoleCutCountersinkAngle = 90
  HoleCutCustomValues = false
  HoleCutDepth = 0
  HoleCutDiameter = 6.1
  HoleCutType = 0
  ModelThread = false
  Profile = -> Binder047
  Reversed = true
  Tapered = false
  TaperedAngle = 90
  ThreadClass = 0
  ThreadDepth = 25
  ThreadDepthType = 0
  ThreadDirection = 0
  ThreadFit = 0
  ThreadSize = 0
  ThreadType = 0
  Threaded = false
  UseCustomThreadClearance = false
FEATURE [PartDesign::Plane] DatumPlane002
  AttachmentOffset = pos=(0,0,52.5) rot=(0,0,1;0rad)
  Length = 640.923
  MapMode = 5
  Placement = pos=(0,0,52.5) rot=(0,0,1;0rad)
  ResizeMode = 0
  Support = -> [XY_Plane027]
  Width = 219.813
  expr: .AttachmentOffset.Base.z = Pad019.Length / 2
FEATURE [PartDesign::Mirrored] Mirrored013
  BaseFeature = -> Hole004
  MirrorPlane = -> DatumPlane002
  Originals = -> [Hole003,Hole004]
FEATURE [PartDesign::Body] Body024
  Group = -> [Binder046,Sketch091,Pad019,Sketch092,Pocket062,Sketch093,Pocket063,Hole,Sketch094,Hole003,Binder047,Hole004,DatumPlane002,Mirrored013]
  Origin = -> Origin027
  Tip = -> Mirrored013
COMPONENT P10 — recipe-attached ("screw_cut", modeled in this document).
Construction recipe (the document's own serialized feature program — sketch geometry with constraints, then the solid features built on it; lengths are millimeters unless a unit is written):

FEATURE [Sketcher::SketchObject] Sketch080
  FullyConstrained = true
  MapMode = 5
  Support = -> [XY_Plane028]
  sketch-geometry (5):
    g0: LineSegment StartX=-3.925 StartY=-3.925 StartZ=0 EndX=-3.925 EndY=3.925 EndZ=0
    g1: LineSegment StartX=-3.925 StartY=3.925 StartZ=0 EndX=3.925 EndY=3.925 EndZ=0
    g2: LineSegment StartX=3.925 StartY=3.925 StartZ=0 EndX=3.925 EndY=-3.925 EndZ=0
    g3: LineSegment StartX=3.925 StartY=-3.925 StartZ=0 EndX=-3.925 EndY=-3.925 EndZ=0
    g4: GeomPoint X=0 Y=1e-16 Z=0
  constraints (12):
    c: Coincident(g0,g1)
    c: Coincident(g1,g2)
    c: Coincident(g2,g3)
    c: Coincident(g3,g0)
    c: Horizontal(g1)
    c: Horizontal(g3)
    c: Vertical(g0)
    c: Vertical(g2)
    c: Symmetric(g1,g0,g4)
    c: Coincident(g4,g-1)
    c: Equal(g2,g1)
    c: DistanceX(g1,g1) = 7.85
FEATURE [PartDesign::Pad] Pad012
  Direction = (0,0,1)
  Length = 5
  Length2 = 10
  Profile = -> Sketch080
  ReferenceAxis = -> Sketch080 [N_Axis]
  Type = 0
FEATURE [PartDesign::Body] Body025  label="screw_cut"
  Group = -> [Sketch080,Pad012]
  Origin = -> Origin028
  Tip = -> Pad012
COMPONENT P11 — recipe-attached ("Body026", modeled in this document).
Construction recipe (the document's own serialized feature program — sketch geometry with constraints, then the solid features built on it; lengths are millimeters unless a unit is written):

FEATURE [PartDesign::SubShapeBinder] Binder045
  BindCopyOnChange = 0
  BindMode = 0
  ClaimChildren = false
  Context = -> Body026 [Binder045.]
  Fuse = false
  MakeFace = true
  OffsetFill = false
  OffsetIntersection = false
  OffsetJoinType = 0
  OffsetOpenResult = false
  PartialLoad = false
  Relative = true
  Support = -> [Unfold_Sketch_bends001]
  _Version = 2
FEATURE [Sketcher::SketchObject] Sketch090
  ExternalGeometry = -> [Binder045]
  FullyConstrained = true
  MapMode = 5
  Support = -> [XY_Plane029]
  sketch-geometry (6):
    g0: Circle CenterX=-130.299 CenterY=-288.152 CenterZ=0 NormalX=0 NormalY=0 NormalZ=1 AngleXU=0 Radius=0.75
    g1: Circle CenterX=-5.33257 CenterY=-171.115 CenterZ=0 NormalX=0 NormalY=0 NormalZ=1 AngleXU=0 Radius=0.75
    g2: Circle CenterX=1.94899 CenterY=-154.34 CenterZ=0 NormalX=0 NormalY=0 NormalZ=1 AngleXU=0 Radius=0.75
    g3: Circle CenterX=1.01143 CenterY=154.331 CenterZ=0 NormalX=0 NormalY=0 NormalZ=1 AngleXU=0 Radius=0.75
    g4: Circle CenterX=-6.36943 CenterY=171.059 CenterZ=0 NormalX=0 NormalY=0 NormalZ=1 AngleXU=0 Radius=0.75
    g5: Circle CenterX=-132.044 CenterY=287.253 CenterZ=0 NormalX=0 NormalY=0 NormalZ=1 AngleXU=0 Radius=0.75
  constraints (12):
    c: Coincident(g0,g-5)
    c: Coincident(g1,g-5)
    c: Coincident(g2,g-6)
    c: Coincident(g3,g-3)
    c: Coincident(g4,g-4)
    c: Coincident(g5,g-4)
    c: Equal(g5,g4)
    c: Equal(g5,g3)
    c: Equal(g5,g2)
    c: Equal(g5,g1)
    c: Equal(g5,g0)
    c: Diameter(g5) = 1.5
FEATURE [Part::Feature] Unfold002
  Placement = pos=(0,0,0) rot=(0.57735,0.57735,0.57735;2.0944rad)
  shape: bbox 220.2 x 682.9 x 0.55 mm, 56 faces (baked)
FEATURE [PartDesign::FeatureAdditivePython] PDW_Add  # link proxy (typed FeaturePython)
  Body = Body026
  ClaimChildren = true
  EditPlacementAdjustments = false
  Enabled = 1
  LinkedObject = -> Unfold002
  MeshTolerance = 0.1
  PatternBaseOffset = 0
  PatternBaseScale = 1
  PatternBaseScaleXYZ = (1,1,1)
  PatternOffsetCut = false
  PatternOffsetIntersection = false
  PatternOffsetJoin = 0
  PatternOffsetMode = 0
  PatternOffsetSelfIntersection = false
  PatternOperation = 0
  PatternOperationDefault = None
  PatternScaleCut = false
  PatternShapeOffset = 0
  PatternShapeScale = 1
  PatternShapeScaleXYZ = (1,1,1)
  PatternToolOffset = 0
  PatternToolScale = 1
  PatternToolScaleXYZ = (1,1,1)
  RefineMesh = true
  ShapeManagement = 0
  ShowMeshProps = false
  ShowOffsetProps = false
  ShowScaleProps = false
  ShowWarnings = true
  TipBaseOffset = 0
  TipBaseScale = 1
  TipBaseScaleXYZ = (1,1,1)
  TipOffsetCut = false
  TipOffsetIntersection = false
  TipOffsetJoin = 0
  TipOffsetMode = 0
  TipOffsetSelfIntersection = false
  TipOperation = 0
  TipOperationDefault = Fuse
  TipScaleCut = false
  TipShapeOffset = 0
  TipShapeScale = 1
  TipShapeScaleXYZ = (1,1,1)
  TipTool = -> Unfold002
  TipToolOffset = 0
  TipToolScale = 1
  TipToolScaleXYZ = (1,1,1)
  Type = Additive
  UsePatternBaseAddSubShape = false
  UsePatternToolAddSubShape = false
  UseTipBaseAddSubShape = false
  UseTipToolAddSubShape = false
  Version = 0.2023.08.13
FEATURE [PartDesign::Pocket] Pocket061
  BaseFeature = -> PDW_Add
  Direction = (0,0,-1)
  Length = 5
  Length2 = 5
  Midplane = true
  Profile = -> Sketch090
  ReferenceAxis = -> Sketch090 [N_Axis]
  Type = 1
FEATURE [PartDesign::Body] Body026
  Group = -> [PDW_Add,Binder045,Sketch090,Pocket061,Unfold002]
  Origin = -> Origin029
  Tip = -> PDW_Add
COMPONENT P12 — geometry summary ("Extrude002"; no construction recipe available for this part):
  bounding box: 10.0 x 3.4 x 3.4 mm
  tessellated surface: 104 triangles
  volume: 91 mm^3 (79% of its bounding box)
  symmetry: 2-fold rotationally symmetric about the y axis; revolution-symmetric about the z axis through its bounding-box center; mirror-symmetric across its y mid-plane
COMPONENT P13 — recipe-attached ("Body001", modeled in this document).
Construction recipe (the document's own serialized feature program — sketch geometry with constraints, then the solid features built on it; lengths are millimeters unless a unit is written):

FEATURE [PartDesign::SubShapeBinder] Binder001
  BindCopyOnChange = 0
  BindMode = 0
  ClaimChildren = false
  Context = -> Body [Binder001.]
  Fuse = false
  MakeFace = true
  OffsetFill = false
  OffsetIntersection = false
  OffsetJoinType = 0
  OffsetOpenResult = false
  PartialLoad = false
  Relative = true
  Support = -> [Sketch005]
  _Version = 2
FEATURE [Sketcher::SketchObject] Sketch009
  ExternalGeometry = -> [Binder001]
  FullyConstrained = true
  MapMode = 5
  Support = -> [XY_Plane]
  expr: Constraints[12] = composit_properties#<<Properties>>.al_thickness
  expr: Constraints[13] = -composit_properties#<<Properties>>.thickness
  sketch-geometry (5):
    g0: LineSegment StartX=0 StartY=-3 StartZ=0 EndX=0 EndY=109.928 EndZ=0
    g1: LineSegment StartX=0 StartY=109.928 StartZ=0 EndX=267.5 EndY=109.928 EndZ=0
    g2: LineSegment StartX=267.5 StartY=109.928 StartZ=0 EndX=267.719 EndY=109.723 EndZ=0
    g3: LineSegment StartX=267.719 StartY=109.723 StartZ=0 EndX=267.719 EndY=-3 EndZ=0
    g4: LineSegment StartX=267.719 StartY=-3 StartZ=0 EndX=0 EndY=-3 EndZ=0
  constraints (15):
    c: PointOnObject(g0,g-2)
    c: Coincident(g0,g1)
    c: Horizontal(g1)
    c: Coincident(g1,g2)
    c: Coincident(g2,g3)
    c: Vertical(g3)
    c: Coincident(g3,g4)
    c: DistanceX(g1,g1) = 267.5
    c: PointOnObject(g1,g-3)
    c: Coincident(g4,g0)
    c: Vertical(g0)
    c: Horizontal(g4)
    c: Distance(g2) = 0.3
    c: DistanceY(g0) = -3
    c: Perpendicular(g-3,g2)
FEATURE [Sketcher::SketchObject] Sketch013
  ExternalGeometry = -> [Sketch]
  FullyConstrained = true
  MapMode = 5
  Support = -> [XY_Plane]
  sketch-geometry (23):
    g0: Circle CenterX=204.177 CenterY=33.9297 CenterZ=0 NormalX=0 NormalY=0 NormalZ=1 AngleXU=0 Radius=1.7
    g1: Circle CenterX=258.844 CenterY=92.3382 CenterZ=0 NormalX=0 NormalY=0 NormalZ=1 AngleXU=0 Radius=1.7
    g2: Circle CenterX=289.784 CenterY=89 CenterZ=0 NormalX=0 NormalY=0 NormalZ=1 AngleXU=0 Radius=1.7
    g3: Circle CenterX=120 CenterY=-5.7 CenterZ=0 NormalX=0 NormalY=0 NormalZ=1 AngleXU=0 Radius=1.7
    g4: Circle CenterX=0 CenterY=-5.7 CenterZ=0 NormalX=0 NormalY=0 NormalZ=1 AngleXU=0 Radius=1.7
    g5: LineSegment StartX=0 StartY=-5.7 StartZ=0 EndX=120 EndY=-5.7 EndZ=0
    g6: LineSegment StartX=204.177 StartY=33.9297 StartZ=0 EndX=258.844 EndY=92.3382 EndZ=0
    g7: LineSegment StartX=289.784 StartY=-41 StartZ=0 EndX=289.784 EndY=89 EndZ=0
    g8: LineSegment StartX=289.784 StartY=89 StartZ=0 EndX=300.084 EndY=89 EndZ=0
    g9: LineSegment StartX=258.844 StartY=92.3382 StartZ=0 EndX=254.682 EndY=96.2332 EndZ=0
    g10: LineSegment StartX=120 StartY=-5.7 StartZ=0 EndX=120 EndY=0 EndZ=0
    g11: Circle CenterX=-120 CenterY=-5.7 CenterZ=0 NormalX=0 NormalY=0 NormalZ=1 AngleXU=0 Radius=1.7
    g12: Circle CenterX=-204.177 CenterY=33.9297 CenterZ=0 NormalX=0 NormalY=0 NormalZ=1 AngleXU=0 Radius=1.7
    g13: Circle CenterX=-258.844 CenterY=92.3382 CenterZ=0 NormalX=0 NormalY=0 NormalZ=1 AngleXU=0 Radius=1.7
    g14: Circle CenterX=-289.784 CenterY=89 CenterZ=0 NormalX=0 NormalY=0 NormalZ=1 AngleXU=0 Radius=1.7
    g15: GeomPoint X=120 Y=-4 Z=0
    g16: LineSegment StartX=168.776 StartY=-3.895 StartZ=0 EndX=204.177 EndY=33.9297 EndZ=0
    g17: LineSegment StartX=258.844 StartY=92.3382 StartZ=0 EndX=294.245 EndY=130.163 EndZ=0
    g18: LineSegment StartX=290.084 StartY=134.058 StartZ=0 EndX=294.245 EndY=130.163 EndZ=0
    g19: LineSegment StartX=168.776 StartY=-3.895 StartZ=0 EndX=164.614 EndY=0 EndZ=0
    g20: GeomPoint X=288.084 Y=89 Z=0
    g21: Circle CenterX=289.784 CenterY=9 CenterZ=0 NormalX=0 NormalY=0 NormalZ=1 AngleXU=0 Radius=1.7
    g22: Circle CenterX=-289.784 CenterY=9 CenterZ=0 NormalX=0 NormalY=0 NormalZ=1 AngleXU=0 Radius=1.7
  constraints (55):
    c: PointOnObject(g4,g-2)
    c: Coincident(g5,g4)
    c: Coincident(g5,g3)
    c: Horizontal(g5)
    c: Coincident(g6,g0)
    c: Coincident(g6,g1)
    c: Coincident(g7,g2)
    c: Vertical(g7)
    c: Coincident(g8,g2)
    c: Horizontal(g8)
    c: Coincident(g9,g1)
    c: Coincident(g10,g3)
    c: PointOnObject(g10,g-1)
    c: Vertical(g10)
    c: Symmetric(g13,g1,g-2)
    c: Symmetric(g12,g0,g-2)
    c: Symmetric(g14,g2,g-2)
    c: Symmetric(g11,g3,g-2)
    c: Equal(g4,g3)
    c: Equal(g4,g0)
    c: Equal(g4,g1)
    c: Equal(g4,g2)
    c: Equal(g4, g11-g14) x4
    c: Diameter(g4) = 3.4
    c: PointOnObject(g15,g3)
    c: PointOnObject(g15,g10)
    c: DistanceY(g15,g10) = 4
    c: Coincident(g16,g0)
    c: Coincident(g17,g1)
    c: Coincident(g18,g17)
    c: Perpendicular(g17,g18)
    c: Parallel(g17,g6)
    c: Parallel(g16,g6)
    c: Coincident(g19,g16)
    c: Perpendicular(g16,g19)
    c: Equal(g16,g17)
    c: Distance(g6) = 80
    c: DistanceY(g7,g7) = 130
    c: DistanceX(g5,g5) = 120
    c: PointOnObject(g20,g2)
    c: PointOnObject(g20,g8)
    c: DistanceX(g20,g8) = 12
    c: Equal(g9,g10)
    c: Parallel(g6,g-4)
    c: Coincident(g19,g-4)
    c: Coincident(g18,g-4)
    c: PointOnObject(g9,g-4)
    c: Perpendicular(g6,g9)
    c: PointOnObject(g8,g-3)
    c: Horizontal(g7,g-3)
    c: PointOnObject(g21,g7)
    c: Equal(g21,g2)
    c: DistanceY(g21,g2) = 80
    c: Equal(g22,g21)
    c: Symmetric(g21,g22,g-2)
FEATURE [Sketcher::SketchObject] Sketch030
  FullyConstrained = true
  MapMode = 5
  Placement = pos=(0,0,0) rot=(1,0,0;1.5708rad)
  Support = -> [XZ_Plane]
  expr: Constraints[22] = BaseBend.radius
  expr: Constraints[23] = BaseBend.thickness
  expr: Constraints[30] = <<base_sketch>>.Constraints.outer_width
  sketch-geometry (18):
    g0: ArcOfCircle CenterX=299.684 CenterY=0 CenterZ=0 NormalX=0 NormalY=0 NormalZ=1 AngleXU=0 Radius=0.1 StartAngle=4.71239 EndAngle=6.28319
    g1: LineSegment StartX=299.784 StartY=-1e-16 StartZ=0 EndX=300.084 EndY=-1e-16 EndZ=0
    g2: ArcOfCircle CenterX=299.684 CenterY=0 CenterZ=0 NormalX=0 NormalY=0 NormalZ=1 AngleXU=0 Radius=0.4 StartAngle=4.71239 EndAngle=6.28319
    g3: ArcOfCircle CenterX=-299.684 CenterY=0 CenterZ=0 NormalX=0 NormalY=0 NormalZ=1 AngleXU=0 Radius=0.4 StartAngle=3.14159 EndAngle=4.71239
    g4: ArcOfCircle CenterX=-299.684 CenterY=0 CenterZ=0 NormalX=0 NormalY=0 NormalZ=1 AngleXU=0 Radius=0.1 StartAngle=3.14159 EndAngle=4.71239
    g5: LineSegment StartX=-300.084 StartY=0 StartZ=0 EndX=-299.784 EndY=0 EndZ=0
    g6: LineSegment StartX=-299.684 StartY=-0.4 StartZ=0 EndX=-285.084 EndY=-0.4 EndZ=0
    g7: LineSegment StartX=-299.684 StartY=-0.1 StartZ=0 EndX=-285.084 EndY=-0.1 EndZ=0
    g8: LineSegment StartX=-285.084 StartY=-0.4 StartZ=0 EndX=-285.084 EndY=-0.1 EndZ=0
    g9: LineSegment StartX=299.684 StartY=-0.1 StartZ=0 EndX=285.084 EndY=-0.1 EndZ=0
    g10: LineSegment StartX=285.084 StartY=-0.1 StartZ=0 EndX=285.084 EndY=-0.4 EndZ=0
    g11: LineSegment StartX=285.084 StartY=-0.4 StartZ=0 EndX=299.684 EndY=-0.4 EndZ=0
    g12: LineSegment StartX=300.084 StartY=-1e-16 StartZ=0 EndX=300.084 EndY=0.1 EndZ=0
    g13: LineSegment StartX=300.084 StartY=0.1 StartZ=0 EndX=299.784 EndY=0.1 EndZ=0
    g14: LineSegment StartX=299.784 StartY=0.1 StartZ=0 EndX=299.784 EndY=-1e-16 EndZ=0
    g15: LineSegment StartX=-299.784 StartY=0 StartZ=0 EndX=-299.784 EndY=0.1 EndZ=0
    g16: LineSegment StartX=-299.784 StartY=0.1 StartZ=0 EndX=-300.084 EndY=0.1 EndZ=0
    g17: LineSegment StartX=-300.084 StartY=0.1 StartZ=0 EndX=-300.084 EndY=0 EndZ=0
  constraints (46):
    c: PointOnObject(g0,g-1)
    c: Coincident(g1,g0)
    c: Coincident(g2,g0)
    c: Coincident(g2,g1)
    c: PointOnObject(g3,g-1)
    c: Coincident(g4,g3)
    c: Coincident(g5,g3)
    c: Coincident(g5,g4)
    c: Horizontal(g6)
    c: Horizontal(g7)
    c: Coincident(g8,g6)
    c: Coincident(g8,g7)
    c: Horizontal(g9)
    c: Coincident(g10,g9)
    c: Coincident(g11,g10)
    c: Horizontal(g11)
    c: Tangent(g11,g2) = -1.5708
    c: Tangent(g9,g0) = 1.5708
    c: Tangent(g7,g4) = -1.5708
    c: Tangent(g6,g3) = -1.5708
    c: Vertical(g8)
    c: Equal(g4,g0)
    c: Radius(g4) = 0.1
    c: DistanceY(g8,g8) = 0.3
    c: Perpendicular(g0,g1)
    c: Horizontal(g1)
    c: Symmetric(g3,g0,g-2)
    c: Horizontal(g5)
    c: Symmetric(g6,g10,g-2)
    c: Vertical(g10)
    c: DistanceX(g3,g1) = 600.168
    c: DistanceX(g10,g1) = 15
    c: Tangent(g2,g12) = -1.5708
    c: Coincident(g12,g13)
    c: Horizontal(g13)
    c: Coincident(g13,g14)
    c: Coincident(g14,g0)
    c: Tangent(g4,g15) = 1.5708
    c: Coincident(g15,g16)
    c: Coincident(g16,g17)
    c: Coincident(g17,g3)
    c: Vertical(g17)
    c: Horizontal(g16)
    c: Vertical(g14)
    c: Horizontal(g13,g15)
    c: DistanceY(g12,g12) = 0.1
FEATURE [Sketcher::SketchObject] Sketch031
  FullyConstrained = true
  MapMode = 5
  Support = -> [XY_Plane]
  expr: Constraints[18] = <<base_sketch>>.Constraints.outer_width - 20 mm
  sketch-geometry (9):
    g0: Circle CenterX=290.084 CenterY=115 CenterZ=0 NormalX=0 NormalY=0 NormalZ=1 AngleXU=0 Radius=1.7
    g1: Circle CenterX=290.084 CenterY=0 CenterZ=0 NormalX=0 NormalY=0 NormalZ=1 AngleXU=0 Radius=1.7
    g2: Circle CenterX=-290.084 CenterY=0 CenterZ=0 NormalX=0 NormalY=0 NormalZ=1 AngleXU=0 Radius=1.7
    g3: Circle CenterX=-290.084 CenterY=115 CenterZ=0 NormalX=0 NormalY=0 NormalZ=1 AngleXU=0 Radius=1.7
    g4: LineSegment StartX=-290.084 StartY=115 StartZ=0 EndX=-290.084 EndY=0 EndZ=0
    g5: LineSegment StartX=-290.084 StartY=0 StartZ=0 EndX=290.084 EndY=0 EndZ=0
    g6: LineSegment StartX=290.084 StartY=0 StartZ=0 EndX=290.084 EndY=115 EndZ=0
    g7: LineSegment StartX=290.084 StartY=115 StartZ=0 EndX=-290.084 EndY=115 EndZ=0
    g8: GeomPoint X=0 Y=57.5 Z=0
  constraints (21):
    c: Coincident(g4,g5)
    c: Coincident(g5,g6)
    c: Coincident(g6,g7)
    c: Coincident(g7,g4)
    c: Horizontal(g5)
    c: Horizontal(g7)
    c: Vertical(g4)
    c: Vertical(g6)
    c: Symmetric(g5,g4,g8)
    c: PointOnObject(g8,g-2)
    c: Coincident(g5,g1)
    c: Coincident(g0,g6)
    c: Coincident(g3,g4)
    c: Coincident(g2,g4)
    c: Equal(g2,g3)
    c: Equal(g2,g0)
    c: Equal(g2,g1)
    c: Diameter(g2) = 3.4
    c: DistanceX(g5,g5) = 580.168
    c: DistanceY(g-1,g1) = 0
    c: DistanceY(g6,g6) = 115
FEATURE [Sketcher::SketchObject] Sketch038
  AttachmentOffset = pos=(0,0,640) rot=(0,0,1;0rad)
  ExternalGeometry = -> [Binder001]
  FullyConstrained = true
  MapMode = 5
  Placement = pos=(0,0,640) rot=(0,0,1;0rad)
  Support = -> [XY_Plane]
  expr: .AttachmentOffset.Base.z = BaseBend.length
  expr: Constraints[0] = <<ULI-3865416>>#<<Properties>>.width + 3 mm
  expr: Constraints[13] = <<ULI-3865416>>#<<Properties>>.length / 2 + 1 mm
  sketch-geometry (6):
    g0: GeomPoint X=267.902 Y=110.358 Z=0
    g1: LineSegment StartX=268.194 StartY=110.085 StartZ=0 EndX=267.902 EndY=110.358 EndZ=0
    g2: LineSegment StartX=267.902 StartY=110.358 StartZ=0 EndX=281 EndY=124.352 EndZ=0
    g3: LineSegment StartX=281 StartY=124.352 StartZ=0 EndX=281.292 EndY=124.079 EndZ=0
    g4: LineSegment StartX=281.292 StartY=124.079 StartZ=0 EndX=268.194 EndY=110.085 EndZ=0
    g5: GeomPoint X=274.597 Y=117.218 Z=0
  constraints (14):
    c: DistanceY(g0,g-3) = 23.7
    c: PointOnObject(g2,g-3)
    c: PointOnObject(g0,g-3)
    c: Coincident(g1,g2)
    c: Coincident(g2,g3)
    c: Coincident(g3,g4)
    c: Coincident(g4,g1)
    c: Parallel(g2,g4)
    c: Symmetric(g2,g1,g5)
    c: Perpendicular(g1,g2)
    c: Coincident(g1,g0)
    c: Distance(g1) = 0.4
    c: Perpendicular(g4,g3)
    c: DistanceX(g2) = 281
FEATURE [PartDesign::CoordinateSystem] Local_CS001
  AttacherType = Attacher::AttachEngine3D
  AttachmentOffset = pos=(164.614,0,0) rot=(0.293211,-0.676028,-0.676028;2.57116rad)
  MapMode = 5
  Placement = pos=(164.614,0,0) rot=(0.293211,-0.676028,-0.676028;2.57116rad)
  Support = -> [XY_Plane]
  expr: .AttachmentOffset.Base.x = <<main_sketch>>.Constraints.inner_width / 2
  expr: .AttachmentOffset.Rotation.Yaw = -(180 deg - <<main_sketch>>.Constraints.angle)
FEATURE [Sketcher::SketchObject] Sketch039
  AttachmentOffset = pos=(0,110,0) rot=(0,0,1;0rad)
  ExternalGeometry = -> [Sketch009]
  FullyConstrained = true
  MapMode = 5
  Placement = pos=(164.614,5.5e-14,110) rot=(-0.293211,0.676028,0.676028;3.71203rad)
  Support = -> [Local_CS001]
  expr: .AttachmentOffset.Base.y = <<Pocket004>>.Length
  sketch-geometry (3):
    g0: LineSegment StartX=0 StartY=0 StartZ=0 EndX=-150.565 EndY=0 EndZ=0
    g1: LineSegment StartX=-150.565 StartY=0 StartZ=0 EndX=-150.565 EndY=11.5554 EndZ=0
    g2: LineSegment StartX=-150.565 StartY=11.5554 StartZ=0 EndX=0 EndY=0 EndZ=0
  constraints (8):
    c: Coincident(g-1,g0)
    c: PointOnObject(g0,g-1)
    c: Coincident(g0,g1)
    c: Vertical(g1)
    c: Coincident(g1,g2)
    c: Coincident(g2,g0)
    c: Vertical(g0,g-3)
    c: Angle(g2) = -0.0765971
FEATURE [Sketcher::SketchObject] Sketch040
  AttachmentOffset = pos=(0,110,0) rot=(0,0,1;0rad)
  ExternalGeometry = -> [Sketch039]
  FullyConstrained = true
  MapMode = 5
  Placement = pos=(164.614,5.5e-14,110) rot=(-0.293211,0.676028,0.676028;3.71203rad)
  Support = -> [Local_CS001]
  expr: AttachmentOffset = <<Sketch039>>.AttachmentOffset
  sketch-geometry (7):
    g0: ArcOfCircle CenterX=-1 CenterY=0 CenterZ=0 NormalX=0 NormalY=0 NormalZ=1 AngleXU=0 Radius=12 StartAngle=1.5708 EndAngle=2.76175
    g1: ArcOfCircle CenterX=-16.7883 CenterY=6.30316 CenterZ=0 NormalX=0 NormalY=0 NormalZ=1 AngleXU=0 Radius=5 StartAngle=4.63579 EndAngle=5.90334
    g2: LineSegment StartX=-17.1709 StartY=1.31782 StartZ=0 EndX=-17.1709 EndY=0 EndZ=0
    g3: LineSegment StartX=-17.1709 StartY=0 StartZ=0 EndX=0 EndY=0 EndZ=0
    g4: LineSegment StartX=0 StartY=0 StartZ=0 EndX=0 EndY=12 EndZ=0
    g5: LineSegment StartX=0 StartY=12 StartZ=0 EndX=-1 EndY=12 EndZ=0
    g6: LineSegment StartX=0 StartY=0 StartZ=0 EndX=-17.1709 EndY=1.31782 EndZ=0
  constraints (18):
    c: Coincident(g3,g4)
    c: Tangent(g1,g0) = 1.5708
    c: Radius(g1) = 5
    c: Radius(g0) = 12  'r'
    c: Coincident(g2,g3)
    c: PointOnObject(g2,g-1)
    c: Vertical(g2)
    c: Coincident(g2,g1)
    c: Coincident(g4,g5)
    c: Horizontal(g5)
    c: PointOnObject(g4,g-2)
    c: PointOnObject(g0,g-1)
    c: Tangent(g0,g5) = -1.5708
    c: DistanceX(g5,g5) = 1
    c: Coincident(g6,g3)
    c: Parallel(g6,g-3)
    c: Coincident(g3,g-1)
    c: Tangent(g1,g6) = 1.5708
FEATURE [Sketcher::SketchObject] Sketch041
  AttachmentOffset = pos=(0,110,0) rot=(0,1,0;-0.818478rad)
  FullyConstrained = true
  MapMode = 5
  Placement = pos=(164.614,5.5e-14,110) rot=(0,-0.707107,-0.707107;3.14159rad)
  Support = -> [Local_CS001]
  expr: .AttachmentOffset.Base.y = <<Sketch039>>.AttachmentOffset.Base.y
  expr: .AttachmentOffset.Rotation.Angle = -<<main_sketch>>.Constraints.angle
  expr: Constraints[12] = Sketch040.Constraints.r
  sketch-geometry (5):
    g0: LineSegment StartX=17.2481 StartY=6.67191e-11 StartZ=0 EndX=-5 EndY=0 EndZ=0
    g1: LineSegment StartX=-5 StartY=0 StartZ=0 EndX=-5 EndY=12 EndZ=0
    g2: LineSegment StartX=-5 StartY=12 StartZ=0 EndX=1 EndY=12 EndZ=0
    g3: ArcOfCircle CenterX=1 CenterY=0 CenterZ=0 NormalX=0 NormalY=0 NormalZ=1 AngleXU=0 Radius=12 StartAngle=0.298532 EndAngle=1.5708
    g4: ArcOfCircle CenterX=17.2481 CenterY=5 CenterZ=0 NormalX=0 NormalY=0 NormalZ=1 AngleXU=0 Radius=5 StartAngle=3.44012 EndAngle=4.71238
  constraints (15):
    c: PointOnObject(g0,g-1)
    c: PointOnObject(g0,g-1)
    c: Coincident(g0,g1)
    c: Vertical(g1)
    c: Coincident(g1,g2)
    c: Horizontal(g2)
    c: PointOnObject(g3,g-1)
    c: Tangent(g3,g2) = 1.5708
    c: Coincident(g4,g0)
    c: Tangent(g4,g3) = 1.5708
    c: Tangent(g4,g-1)
    c: DistanceX(g2) = 1
    c: Radius(g3) = 12
    c: DistanceX(g0) = -5
    c: Radius(g4) = 5
FEATURE [Sketcher::SketchObject] Sketch046
  ExternalGeometry = -> [Binder001]
  FullyConstrained = true
  MapMode = 5
  Support = -> [XY_Plane]
  sketch-geometry (5):
    g0: LineSegment StartX=291.385 StartY=131.058 StartZ=0 EndX=281.744 EndY=120.757 EndZ=0
    g1: LineSegment StartX=281.744 StartY=120.757 StartZ=0 EndX=267.635 EndY=120.757 EndZ=0
    g2: LineSegment StartX=289.195 StartY=133.108 StartZ=0 EndX=291.385 EndY=131.058 EndZ=0
    g3: LineSegment StartX=291.385 StartY=131.058 StartZ=0 EndX=291.385 EndY=134.058 EndZ=0
    g4: GeomPoint X=277.635 Y=120.757 Z=0
  constraints (17):
    c: Coincident(g1,g0)
    c: Horizontal(g1)
    c: Parallel(g0,g-3)
    c: DistanceY(g0,g-3) = 3
    c: PointOnObject(g2,g-3)
    c: Coincident(g2,g0)
    c: Coincident(g2,g3)
    c: Vertical(g3)
    c: Horizontal(g-3,g3)
    c: Equal(g3,g2)
    c: Perpendicular(g-3,g2)
    c: PointOnObject(g4,g-3)
    c: PointOnObject(g4,g1)
    c: DistanceX(g1,g4) = 10
    c: Equal(g1,g0)
    c: DistanceY(g0,g-3) = 13.3011
    c: DistanceX(g1,g1) = 14.109
FEATURE [PartDesign::CoordinateSystem] Local_CS003
  AttacherType = Attacher::AttachEngine3D
  AttachmentOffset = pos=(0,-50,0) rot=(0,0,1;3.14159rad)
  MapMode = 6
  Placement = pos=(277.635,120.757,50) rot=(-0.293211,0.676028,0.676028;3.71203rad)
  Support = -> [Local_CS001,Sketch046]
FEATURE [Sketcher::SketchObject] Sketch047
  ExternalGeometry = -> [Sketch046]
  FullyConstrained = true
  MapMode = 5
  Placement = pos=(277.635,120.757,50) rot=(-0.293211,0.676028,0.676028;3.71203rad)
  Support = -> [Local_CS003]
  sketch-geometry (5):
    g0: LineSegment StartX=0 StartY=-9.5 StartZ=0 EndX=3.2 EndY=-9.5 EndZ=0
    g1: LineSegment StartX=3.2 StartY=-9.5 StartZ=0 EndX=3.2 EndY=9.5 EndZ=0
    g2: LineSegment StartX=3.2 StartY=9.5 StartZ=0 EndX=0 EndY=9.5 EndZ=0
    g3: LineSegment StartX=0 StartY=9.5 StartZ=0 EndX=0 EndY=-9.5 EndZ=0
    g4: GeomPoint X=1.6 Y=0 Z=0
  constraints (13):
    c: Coincident(g0,g1)
    c: Coincident(g1,g2)
    c: Coincident(g2,g3)
    c: Coincident(g3,g0)
    c: Horizontal(g0)
    c: Horizontal(g2)
    c: Vertical(g1)
    c: Vertical(g3)
    c: Vertical(g-3,g0)
    c: DistanceY(g3,g3) = 19
    c: DistanceX(g0,g0) = 3.2
    c: Symmetric(g0,g1,g4)
    c: PointOnObject(g4,g-1)
FEATURE [Sketcher::SketchObject] Sketch048
  FullyConstrained = true
  MapMode = 5
  Placement = pos=(277.635,120.757,50) rot=(-0.293211,0.676028,0.676028;3.71203rad)
  Support = -> [Local_CS003]
  sketch-geometry (2):
    g0: Circle CenterX=-10 CenterY=-5.5 CenterZ=0 NormalX=0 NormalY=0 NormalZ=1 AngleXU=0 Radius=1.7
    g1: Circle CenterX=-10 CenterY=5.5 CenterZ=0 NormalX=0 NormalY=0 NormalZ=1 AngleXU=0 Radius=1.7
  constraints (5):
    c: Symmetric(g0,g1,g-1)
    c: Equal(g0,g1)
    c: Diameter(g0) = 3.4
    c: DistanceY(g0,g1) = 11
    c: DistanceX(g1) = -10
FEATURE [PartDesign::SubShapeBinder] Binder037
  BindCopyOnChange = 0
  BindMode = 0
  ClaimChildren = true
  Context = -> Body [Binder037.]
  Fuse = false
  MakeFace = true
  OffsetFill = false
  OffsetIntersection = false
  OffsetJoinType = 0
  OffsetOpenResult = false
  PartialLoad = false
  Relative = true
  Support = -> [Sketch]
  _Version = 2
  expr: Support = <<base_sketch>>._self
FEATURE [PartDesign::FeaturePython] BaseBend  # WARN: FeaturePython — macro-defined, semantics opaque (R4)
  BendSide = 0
  BendSketch = -> Binder037
  MidPlane = false
  Reverse = false
  length = 640
  radius = 0.1
  thickness = 0.3
FEATURE [PartDesign::FeaturePython] Bend001  # WARN: FeaturePython — macro-defined, semantics opaque (R4)
  AutoMiter = false
  BaseFeature = -> BaseBend
  BendType = 0
  LengthList = [9]
  LengthSpec = 1
  ReliefFactor = 0.7
  UseReliefFactor = false
  angle = 90
  baseObject = -> BaseBend [Edge50,Edge66,Edge82]
  bendAList = [90]
  extend1 = 0
  extend2 = 0
  gap1 = 35
  gap2 = 35
  invert = false
  kfactor = 0.5
  length = 9
  maxExtendDist = 5
  minGap = 0.1
  minReliefGap = 1
  miterangle1 = 0
  miterangle2 = 0
  offset = 0
  radius = 0.1
  reliefType = 0
  reliefd = 1
  reliefw = 0.8
  sketchflip = false
  sketchinvert = false
  unfold = false
  expr: baseObject = tuple(BaseBend._self; list(<<Edge50>>; <<Edge66>>; <<Edge82>>))
  expr: gap2 = gap1
  expr: radius = BaseBend.radius
FEATURE [PartDesign::FeaturePython] Bend003  # WARN: FeaturePython — macro-defined, semantics opaque (R4)
  AutoMiter = true
  BaseFeature = -> Bend001
  BendType = 0
  LengthList = [15]
  LengthSpec = 0
  ReliefFactor = 0.7
  UseReliefFactor = false
  angle = 90
  baseObject = -> Bend001 [Edge131,Edge238]
  bendAList = [90]
  extend1 = 0
  extend2 = 0
  gap1 = 20
  gap2 = 3
  invert = false
  kfactor = 0.5
  length = 15
  maxExtendDist = 5
  minGap = 0.1
  minReliefGap = 1
  miterangle1 = 0
  miterangle2 = 0
  offset = 0
  radius = 0.1
  reliefType = 0
  reliefd = 1
  reliefw = 0.8
  sketchflip = false
  sketchinvert = false
  unfold = false
  expr: radius = BaseBend.radius
FEATURE [PartDesign::SubShapeBinder] Binder039
  BindCopyOnChange = 0
  BindMode = 0
  ClaimChildren = false
  Context = -> Body [Binder039.]
  Fuse = false
  MakeFace = true
  OffsetFill = false
  OffsetIntersection = false
  OffsetJoinType = 0
  OffsetOpenResult = false
  PartialLoad = false
  Relative = true
  Support = -> [Body019[Sketch064.]]
  _Version = 2
FEATURE [PartDesign::Pocket] Pocket047
  BaseFeature = -> Bend003
  Direction = (-0.730107,0.683333,0)
  Length = 5
  Length2 = 5
  Midplane = true
  Profile = -> Binder039
  Type = 0
FEATURE [PartDesign::Pad] Pad005
  BaseFeature = -> Pocket047
  Direction = (0,0,-1)
  Length = 6
  Length2 = 10
  Profile = -> Bend003 [Face113,Face120,Face124,Face137,Face145,Face15,Face25,Face26,Face33,Face34]
  Type = 0
FEATURE [PartDesign::Pocket] Pocket022
  BaseFeature = -> Pad005
  Direction = (0,0,-1)
  Length = 5
  Length2 = 5
  Profile = -> Sketch031
  ReferenceAxis = -> Sketch031 [N_Axis]
  Type = 0
FEATURE [PartDesign::Pocket] Pocket008
  BaseFeature = -> Pocket022
  Direction = (0,0,-1)
  Length = 5
  Length2 = 5
  Profile = -> Sketch013
  ReferenceAxis = -> Sketch013 [N_Axis]
  Reversed = true
  Type = 1
FEATURE [PartDesign::Boolean] Boolean
  BaseFeature = -> Pocket008
  Group = -> [Compound]
  Type = 1
FEATURE [PartDesign::Pocket] Pocket004
  BaseFeature = -> Boolean
  Direction = (0,0,-1)
  Length = 110
  Length2 = 5
  Profile = -> Sketch009
  ReferenceAxis = -> Sketch009 [N_Axis]
  Reversed = true
  Type = 0
FEATURE [PartDesign::Mirrored] Mirrored002
  BaseFeature = -> Pocket004
  MirrorPlane = -> Sketch009 [V_Axis]
  Originals = -> [Pocket004]
  Refine = true
FEATURE [PartDesign::Pocket] Pocket027
  BaseFeature = -> Mirrored002
  Direction = (0.730107,-0.683333,4e-16)
  Length = 5
  Length2 = 5
  Profile = -> Sketch039
  ReferenceAxis = -> Sketch039 [N_Axis]
  Type = 0
FEATURE [PartDesign::Pocket] Pocket028
  BaseFeature = -> Pocket027
  Direction = (0.730107,-0.683333,4e-16)
  Length = 5
  Length2 = 5
  Midplane = true
  Profile = -> Sketch040
  ReferenceAxis = -> Sketch040 [N_Axis]
  Type = 0
FEATURE [PartDesign::Pocket] Pocket029
  BaseFeature = -> Pocket028
  Direction = (-4e-16,-1,3e-16)
  Length = 5
  Length2 = 0.2
  Profile = -> Sketch041
  ReferenceAxis = -> Sketch041 [N_Axis]
  Type = 4
FEATURE [PartDesign::Mirrored] Mirrored007
  BaseFeature = -> Pocket029
  MirrorPlane = -> YZ_Plane
  Originals = -> [Pocket027,Pocket028,Pocket029,Pocket047]
  Refine = true
FEATURE [PartDesign::Body] Body  label="Body_material_0.30ansi"
  Group = -> [BaseBend,Binder001,Bend001,Sketch013,Binder037,Binder039,Bend003,Pocket047,Sketch030,Pad005,Sketch031,Pocket022,Sketch038,Pocket008,Boolean,Sketch009,Pocket004,Mirrored002,Local_CS001,Sketch039,Sketch040,Pocket027,Pocket028,Sketch041,Pocket029,Mirrored007,Sketch046,Sketch047,Sketch048,Local_CS003]
  Origin = -> Origin
  Tip = -> Pocket029
COMPONENT P14 — same part as P13; its construction recipe is shown at P13.
COMPONENT P15 — recipe-attached ("top_material_0.30ansi001", modeled in this document).
Construction recipe (the document's own serialized feature program — sketch geometry with constraints, then the solid features built on it; lengths are millimeters unless a unit is written):

FEATURE [PartDesign::SubShapeBinder] Binder010
  BindCopyOnChange = 0
  BindMode = 0
  ClaimChildren = true
  Context = -> Body003 [Binder010.]
  Fuse = false
  MakeFace = true
  OffsetFill = false
  OffsetIntersection = false
  OffsetJoinType = 0
  OffsetOpenResult = false
  PartialLoad = false
  Relative = false
  Support = -> [Populate009]
  _Version = 2
FEATURE [PartDesign::SubShapeBinder] Binder012
  BindCopyOnChange = 0
  BindMode = 0
  ClaimChildren = true
  Context = -> Part002 [Body003.Binder012.]
  Fuse = false
  MakeFace = true
  OffsetFill = false
  OffsetIntersection = false
  OffsetJoinType = 0
  OffsetOpenResult = false
  PartialLoad = false
  Relative = true
  Support = -> [Body[Pocket008.Sketch013.]]
  _Version = 2
FEATURE [Sketcher::SketchObject] Sketch027
  FullyConstrained = true
  MapMode = 5
  Support = -> [XY_Plane003]
FEATURE [Sketcher::SketchObject] Sketch029
  FullyConstrained = true
  MapMode = 5
  Placement = pos=(0,0,0) rot=(1,0,0;1.5708rad)
  Support = -> [XZ_Plane003]
FEATURE [Sketcher::SketchObject] Sketch043
  AttachmentOffset = pos=(0,0,290) rot=(0,0,1;0rad)
  FullyConstrained = true
  MapMode = 5
  Placement = pos=(290,0,0) rot=(0.57735,0.57735,0.57735;2.0944rad)
  Support = -> [YZ_Plane003]
  expr: Constraints[10] = <<main_sketch>>.Constraints.length
  sketch-geometry (5):
    g0: LineSegment StartX=124.058 StartY=0 StartZ=0 EndX=164.058 EndY=0 EndZ=0
    g1: LineSegment StartX=164.058 StartY=0 StartZ=0 EndX=164.058 EndY=30 EndZ=0
    g2: LineSegment StartX=164.058 StartY=30 StartZ=0 EndX=124.058 EndY=30 EndZ=0
    g3: LineSegment StartX=124.058 StartY=30 StartZ=0 EndX=124.058 EndY=0 EndZ=0
    g4: GeomPoint X=134.058 Y=0 Z=0
  constraints (14):
    c: Coincident(g0,g1)
    c: Coincident(g1,g2)
    c: Coincident(g2,g3)
    c: Coincident(g3,g0)
    c: Horizontal(g0)
    c: Horizontal(g2)
    c: Vertical(g1)
    c: Vertical(g3)
    c: PointOnObject(g0,g-1)
    c: PointOnObject(g4,g-1)
    c: DistanceX(g4) = 134.058
    c: DistanceX(g0,g4) = 10
    c: DistanceY(g0,g2) = 30
    c: DistanceX(g0,g0) = 40
FEATURE [PartDesign::SubShapeBinder] Binder042
  BindCopyOnChange = 0
  BindMode = 0
  ClaimChildren = false
  Context = -> Part002 [Body003.Binder042.]
  Fuse = false
  MakeFace = true
  OffsetFill = false
  OffsetIntersection = false
  OffsetJoinType = 0
  OffsetOpenResult = false
  PartialLoad = false
  Placement = pos=(0,0,0) rot=(0.57735,0.57735,0.57735;2.0944rad)
  Relative = false
  Support = -> [Sketch011]
  _Version = 2
  expr: Support = <<top_BaseSketch>>._self
FEATURE [PartDesign::FeaturePython] BaseBend002  label="top_BaseBend"  # WARN: FeaturePython — macro-defined, semantics opaque (R4)
  BendSide = 0
  BendSketch = -> Binder042
  MidPlane = true
  Reverse = false
  length = 580.168
  radius = 0.1
  thickness = 0.3
  expr: length = <<main_sketch>>.Constraints.outer_width
FEATURE [PartDesign::Pocket] Pocket021
  BaseFeature = -> BaseBend002
  Direction = (0,0,-1)
  Length = 1
  Length2 = 5
  Profile = -> Sketch026
  ReferenceAxis = -> Sketch026 [N_Axis]
  Reversed = true
  Type = 0
FEATURE [PartDesign::Mirrored] Mirrored005
  BaseFeature = -> Pocket021
  MirrorPlane = -> YZ_Plane003
  Originals = -> [Pocket021]
FEATURE [PartDesign::FeaturePython] Bend007  # WARN: FeaturePython — macro-defined, semantics opaque (R4)
  AutoMiter = false
  BaseFeature = -> Mirrored005
  BendType = 0
  LengthList = [20]
  LengthSpec = 0
  ReliefFactor = 0.7
  UseReliefFactor = false
  angle = 90
  baseObject = -> Mirrored005 [Edge2,Edge5,Edge8,Edge11,Edge14,Edge17]
  bendAList = [90]
  extend1 = 0
  extend2 = 0
  gap1 = 0
  gap2 = 0
  invert = false
  kfactor = 0.5
  length = 20
  maxExtendDist = 5
  minGap = 0.1
  minReliefGap = 1
  miterangle1 = 0
  miterangle2 = 0
  offset = 0
  radius = 0.1
  reliefType = 0
  reliefd = 1
  reliefw = 0.8
  sketchflip = false
  sketchinvert = false
  unfold = false
  expr: radius = <<top_BaseBend>>.radius
FEATURE [PartDesign::Pocket] Pocket009
  BaseFeature = -> Bend007
  Direction = (0,0,-1)
  Length = 5
  Length2 = 5
  Midplane = true
  Profile = -> Binder012
  Refine = true
  Type = 1
FEATURE [PartDesign::Pocket] Pocket007
  BaseFeature = -> Pocket009
  Direction = (0,0,-1)
  Length = 5
  Length2 = 5
  Midplane = true
  Profile = -> Binder010
  Type = 1
FEATURE [PartDesign::Pocket] Pocket031
  BaseFeature = -> Pocket007
  Direction = (-0.730107,0.683333,-1e-16)
  Length = 5
  Length2 = 5
  Profile = -> Sketch045
  ReferenceAxis = -> Sketch045 [N_Axis]
  Reversed = true
  Type = 0
FEATURE [PartDesign::Mirrored] Mirrored008
  BaseFeature = -> Pocket031
  MirrorPlane = -> YZ_Plane003
  Originals = -> [Pocket031]
FEATURE [PartDesign::Boolean] Boolean006
  BaseFeature = -> Mirrored008
  Group = -> [Compound012]
  Type = 1
  expr: Group = <<top_cut1>>._self
FEATURE [PartDesign::Body] Body003  label="top_material_0.30ansi"
  Group = -> [BaseBend002,Sketch027,Sketch029,Sketch043,Pocket021,Mirrored005,Bend007,Pocket009,Pocket007,Pocket031,Mirrored008,Boolean006,Binder010,Binder042,Binder012]
  Origin = -> Origin003
  Tip = -> BaseBend002
COMPONENT P16 — recipe-attached ("sink_hand001", modeled in this document).
Construction recipe (the document's own serialized feature program — sketch geometry with constraints, then the solid features built on it; lengths are millimeters unless a unit is written):

FEATURE [PartDesign::SubShapeBinder] Binder014
  BindCopyOnChange = 0
  BindMode = 0
  ClaimChildren = true
  Context = -> Part [Body006.Binder014.]
  Fuse = false
  MakeFace = true
  OffsetFill = false
  OffsetIntersection = false
  OffsetJoinType = 0
  OffsetOpenResult = false
  PartialLoad = false
  Relative = true
  Support = -> [Body001[Pocket.Sketch003.]]
  _Version = 2
FEATURE [Sketcher::SketchObject] Sketch016
  ExternalGeometry = -> [Binder014]
  FullyConstrained = true
  MapMode = 5
  Support = -> [XY_Plane006]
  sketch-geometry (8):
    g0: LineSegment StartX=282.165 StartY=128.763 StartZ=0 EndX=287.147 EndY=134.115 EndZ=0
    g1: LineSegment StartX=0 StartY=120.796 StartZ=0 EndX=263.866 EndY=120.796 EndZ=0
    g2: LineSegment StartX=286.415 StartY=135.796 StartZ=0 EndX=0 EndY=135.796 EndZ=0
    g3: LineSegment StartX=0 StartY=120.796 StartZ=0 EndX=0 EndY=135.796 EndZ=0
    g4: ArcOfCircle CenterX=286.415 CenterY=134.796 CenterZ=0 NormalX=0 NormalY=0 NormalZ=1 AngleXU=0 Radius=1 StartAngle=5.53361 EndAngle=7.85398
    g5: GeomPoint X=288.712 Y=135.796 Z=0
    g6: ArcOfCircle CenterX=263.866 CenterY=145.796 CenterZ=0 NormalX=0 NormalY=0 NormalZ=1 AngleXU=0 Radius=25 StartAngle=4.71239 EndAngle=5.53361
    g7: GeomPoint X=274.75 Y=120.796 Z=0
  constraints (20):
    c: Parallel(g0,g-3)
    c: DistanceY(g-3,g5) = 1
    c: PointOnObject(g2,g-2)
    c: Coincident(g3,g1)
    c: Coincident(g3,g2)
    c: PointOnObject(g1,g-2)
    c: PointOnObject(g5,g0)
    c: PointOnObject(g5,g2)
    c: Tangent(g0,g4) = -1.5708
    c: Tangent(g2,g4) = -1.5708
    c: PointOnObject(g7,g0)
    c: PointOnObject(g7,g1)
    c: Tangent(g0,g6) = -1.5708
    c: Tangent(g1,g6) = -1.5708
    c: Distance(g5,g-3) = 1
    c: Horizontal(g2)
    c: Horizontal(g1)
    c: Radius(g4) = 1
    c: DistanceY(g3,g3) = 15
    c: Radius(g6) = 25
FEATURE [PartDesign::Pad] Pad001
  Direction = (0,0,1)
  Length = 3
  Length2 = 10
  Profile = -> Sketch016
  ReferenceAxis = -> Sketch016 [N_Axis]
  Type = 0
FEATURE [PartDesign::SubShapeBinder] Binder015
  BindCopyOnChange = 0
  BindMode = 0
  ClaimChildren = false
  Context = -> Part [Body006.Binder015.]
  Fuse = false
  MakeFace = true
  OffsetFill = false
  OffsetIntersection = false
  OffsetJoinType = 0
  OffsetOpenResult = false
  PartialLoad = false
  Relative = true
  Support = -> [Body001[Pocket011.Sketch017.]]
  _Version = 2
FEATURE [PartDesign::Pocket] Pocket012
  BaseFeature = -> Pad001
  Direction = (0,-2.7e-15,-1)
  Length = 5
  Length2 = 5
  Profile = -> Binder015
  Reversed = true
  Type = 0
FEATURE [PartDesign::Mirrored] Mirrored003
  BaseFeature = -> Pocket012
  MirrorPlane = -> Sketch016 [V_Axis]
  Originals = -> [Pad001,Pocket012]
  Refine = true
FEATURE [PartDesign::Body] Body006  label="sink_hand"
  Group = -> [Binder014,Sketch016,Pad001,Pocket012,Mirrored003,Binder015]
  Origin = -> Origin006
  Placement = pos=(0,-0.0522642,0.497261) rot=(1,0,0;0.10472rad)
  Tip = -> Mirrored003
  expr: Placement = placement(vector(0; 0; 0); rotation(0; 0; 6)) * placement(vector(0; 0; 0.5); rotation(0; 0; 0))
COMPONENT P17 — recipe-attached ("sink", modeled in this document).
Construction recipe (the document's own serialized feature program — sketch geometry with constraints, then the solid features built on it; lengths are millimeters unless a unit is written):

FEATURE [Sketcher::SketchObject] Sketch007
  FullyConstrained = false
  MapMode = 5
  Placement = pos=(0,0,0) rot=(1,0,0;1.5708rad)
  Support = -> [XZ_Plane001]
  expr: Constraints[10] = BaseBend001.length
  sketch-geometry (5):
    g0: LineSegment StartX=-500 StartY=191.028 StartZ=0 EndX=-500 EndY=87 EndZ=0
    g1: LineSegment StartX=-500 StartY=87 StartZ=0 EndX=500 EndY=87 EndZ=0
    g2: LineSegment StartX=500 StartY=87 StartZ=0 EndX=500 EndY=191.028 EndZ=0
    g3: LineSegment StartX=500 StartY=191.028 StartZ=0 EndX=-500 EndY=191.028 EndZ=0
    g4: GeomPoint X=0 Y=139.014 Z=0
  constraints (12):
    c: Coincident(g0,g1)
    c: Coincident(g1,g2)
    c: Coincident(g2,g3)
    c: Coincident(g3,g0)
    c: Horizontal(g1)
    c: Horizontal(g3)
    c: Vertical(g0)
    c: Vertical(g2)
    c: Symmetric(g1,g0,g4)
    c: PointOnObject(g4,g-2)
    c: DistanceX(g1,g1) = 1000
    c: DistanceY(g1) = 87
FEATURE [Part::Part2DObjectPython] Line  # Draft 2D object (typed FeaturePython)
  Area = 0
  Bend_Angle = 6.03317
  ChamferSize = 0
  Closed = false
  End = (290.084,134.058,14.0901)
  FilletRadius = 0
  Length = 184.154
  MakeFace = true
  Points = (2) [(164.614,0,0),(290.084,134.058,14.0901)]
  SideAngle = 4.1058
  Start = (164.614,0,0)
  Subdivisions = 0
  expr: .End.x = Sketch005.Constraints.outer_width / 2
  expr: .End.y = <<sink_base>>.Constraints.length
  expr: .End.z = <<sink_base>>.Constraints.sink_difference
  expr: .Start.x = <<main_sketch>>.Constraints.inner_width / 2
  expr: Bend_Angle = asin(.End.z / .End.y)
  expr: SideAngle = asin(.End.z / (.End.y + (.End.x - .Start.x) / 2))
FEATURE [PartDesign::SubShapeBinder] Binder
  BindCopyOnChange = 0
  BindMode = 0
  ClaimChildren = false
  Context = -> Part [Body001.Binder.]
  Fuse = false
  MakeFace = true
  OffsetFill = false
  OffsetIntersection = false
  OffsetJoinType = 0
  OffsetOpenResult = false
  PartialLoad = false
  Relative = false
  Support = -> [Sketch005]
  _Version = 2
FEATURE [Sketcher::SketchObject] Sketch006
  ExternalGeometry = -> [Binder]
  FullyConstrained = true
  MapMode = 5
  Support = -> [XY_Plane001]
  sketch-geometry (1):
    g0: LineSegment StartX=161.19 StartY=0 StartZ=0 EndX=286.66 EndY=134.058 EndZ=0
  constraints (5):
    c: PointOnObject(g0,g-1)
    c: Horizontal(g0,g-3)
    c: Parallel(g-3,g0)
    c: Distance(g0,g-3) = 2.5
    c: DistanceX(g0) = 286.66  'max_right'
FEATURE [Sketcher::SketchObject] Sketch001  label="sink_base"
  ExternalGeometry = -> [Binder]
  FullyConstrained = true
  MapMode = 5
  Placement = pos=(0,0,0) rot=(0.57735,0.57735,0.57735;2.0944rad)
  Support = -> [YZ_Plane001]
  sketch-geometry (4):
    g0: LineSegment StartX=0 StartY=0 StartZ=0 EndX=0 EndY=90 EndZ=0
    g1: LineSegment StartX=0 StartY=0 StartZ=0 EndX=134.058 EndY=14.0901 EndZ=0
    g2: ArcOfCircle CenterX=2.5 CenterY=2.77653 CenterZ=0 NormalX=0 NormalY=0 NormalZ=1 AngleXU=0 Radius=2.5 StartAngle=3.14159 EndAngle=4.81711
    g3: GeomPoint X=2.76132 Y=0.290227 Z=0
  constraints (13):
    c: Vertical(g0)
    c: Coincident(g1,g0)
    c: Angle(g1) = 0.10472  'angle'
    c: DistanceY(g0,g0) = 90
    c: Coincident(g0,g-1)
    c: Vertical(g-3,g1)
    c: DistanceX(g1) = 134.058  'length'
    c: DistanceY(g1) = 14.0901  'sink_difference'
    c: Tangent(g2,g1) = -1.5708
    c: Tangent(g2,g0) = 1.5708
    c: Radius(g2) = 2.5
    c: DistanceX(g2) = 2.76132
    c: Coincident(g3,g2)
FEATURE [Sketcher::SketchObject] Sketch004
  ExternalGeometry = -> [Sketch001]
  FullyConstrained = false
  MapMode = 7
  Placement = pos=(164.614,-1.42e-14,0) rot=(0.880512,-0.347772,-0.322108;1.77331rad)
  Support = -> [Line]
  sketch-geometry (9):
    g0: LineSegment StartX=-120.186 StartY=8.60659 StartZ=0 EndX=0 EndY=0 EndZ=0
    g1: ArcOfCircle CenterX=-2.5 CenterY=2.68543 CenterZ=0 NormalX=0 NormalY=0 NormalZ=1 AngleXU=0 Radius=2.5 StartAngle=4.6409 EndAngle=6.28319
    g2: LineSegment StartX=-2.67857 StartY=0.191814 StartZ=0 EndX=-2.64286 EndY=0.690537 EndZ=0
    g3: LineSegment StartX=-0.5 StartY=2.68543 StartZ=0 EndX=-0.5 EndY=11.4404 EndZ=0
    g4: LineSegment StartX=-0.5 StartY=11.4404 StartZ=0 EndX=-1.1e-15 EndY=11.4404 EndZ=0
    g5: LineSegment StartX=-1.1e-15 StartY=11.4404 StartZ=0 EndX=0 EndY=2.68543 EndZ=0
    g6: ArcOfCircle CenterX=-2.5 CenterY=2.68543 CenterZ=0 NormalX=0 NormalY=0 NormalZ=1 AngleXU=0 Radius=2 StartAngle=4.6409 EndAngle=6.28319
    g7: LineSegment StartX=0 StartY=2.68543 StartZ=0 EndX=-2.5 EndY=2.68543 EndZ=0
    g8: LineSegment StartX=-2.67857 StartY=0.191814 StartZ=0 EndX=-2.5 EndY=2.68543 EndZ=0
  constraints (21):
    c: Coincident(g0,g-3)
    c: Coincident(g0,g-1)
    c: Tangent(g1,g-2) = -1.5708
    c: Radius(g1) = 2.5
    c: Tangent(g1,g0) = -1.5708
    c: Coincident(g2,g1)
    c: Vertical(g3)
    c: Coincident(g4,g3)
    c: Coincident(g5,g4)
    c: Tangent(g5,g1) = 1.5708
    c: Horizontal(g4)
    c: Perpendicular(g1,g2)
    c: Coincident(g6,g1)
    c: Coincident(g6,g2)
    c: Tangent(g6,g3) = -1.5708
    c: Radius(g6) = 2
    c: Coincident(g7,g1)
    c: Coincident(g7,g1)
    c: Coincident(g8,g1)
    c: Coincident(g8,g1)
    c: Angle(g8,g7) = 1.64228
FEATURE [PartDesign::SubShapeBinder] Binder014
  BindCopyOnChange = 0
  BindMode = 0
  ClaimChildren = true
  Context = -> Part [Body006.Binder014.]
  Fuse = false
  MakeFace = true
  OffsetFill = false
  OffsetIntersection = false
  OffsetJoinType = 0
  OffsetOpenResult = false
  PartialLoad = false
  Relative = true
  Support = -> [Body001[Pocket.Sketch003.]]
  _Version = 2
FEATURE [Sketcher::SketchObject] Sketch016
  ExternalGeometry = -> [Binder014]
  FullyConstrained = true
  MapMode = 5
  Support = -> [XY_Plane006]
  sketch-geometry (8):
    g0: LineSegment StartX=282.165 StartY=128.763 StartZ=0 EndX=287.147 EndY=134.115 EndZ=0
    g1: LineSegment StartX=0 StartY=120.796 StartZ=0 EndX=263.866 EndY=120.796 EndZ=0
    g2: LineSegment StartX=286.415 StartY=135.796 StartZ=0 EndX=0 EndY=135.796 EndZ=0
    g3: LineSegment StartX=0 StartY=120.796 StartZ=0 EndX=0 EndY=135.796 EndZ=0
    g4: ArcOfCircle CenterX=286.415 CenterY=134.796 CenterZ=0 NormalX=0 NormalY=0 NormalZ=1 AngleXU=0 Radius=1 StartAngle=5.53361 EndAngle=7.85398
    g5: GeomPoint X=288.712 Y=135.796 Z=0
    g6: ArcOfCircle CenterX=263.866 CenterY=145.796 CenterZ=0 NormalX=0 NormalY=0 NormalZ=1 AngleXU=0 Radius=25 StartAngle=4.71239 EndAngle=5.53361
    g7: GeomPoint X=274.75 Y=120.796 Z=0
  constraints (20):
    c: Parallel(g0,g-3)
    c: DistanceY(g-3,g5) = 1
    c: PointOnObject(g2,g-2)
    c: Coincident(g3,g1)
    c: Coincident(g3,g2)
    c: PointOnObject(g1,g-2)
    c: PointOnObject(g5,g0)
    c: PointOnObject(g5,g2)
    c: Tangent(g0,g4) = -1.5708
    c: Tangent(g2,g4) = -1.5708
    c: PointOnObject(g7,g0)
    c: PointOnObject(g7,g1)
    c: Tangent(g0,g6) = -1.5708
    c: Tangent(g1,g6) = -1.5708
    c: Distance(g5,g-3) = 1
    c: Horizontal(g2)
    c: Horizontal(g1)
    c: Radius(g4) = 1
    c: DistanceY(g3,g3) = 15
    c: Radius(g6) = 25
FEATURE [PartDesign::Pad] Pad001
  Direction = (0,0,1)
  Length = 3
  Length2 = 10
  Profile = -> Sketch016
  ReferenceAxis = -> Sketch016 [N_Axis]
  Type = 0
FEATURE [PartDesign::SubShapeBinder] Binder015
  BindCopyOnChange = 0
  BindMode = 0
  ClaimChildren = false
  Context = -> Part [Body006.Binder015.]
  Fuse = false
  MakeFace = true
  OffsetFill = false
  OffsetIntersection = false
  OffsetJoinType = 0
  OffsetOpenResult = false
  PartialLoad = false
  Relative = true
  Support = -> [Body001[Pocket011.Sketch017.]]
  _Version = 2
FEATURE [PartDesign::Pocket] Pocket012
  BaseFeature = -> Pad001
  Direction = (0,-2.7e-15,-1)
  Length = 5
  Length2 = 5
  Profile = -> Binder015
  Reversed = true
  Type = 0
FEATURE [PartDesign::Mirrored] Mirrored003
  BaseFeature = -> Pocket012
  MirrorPlane = -> Sketch016 [V_Axis]
  Originals = -> [Pad001,Pocket012]
  Refine = true
FEATURE [PartDesign::Body] Body006  label="sink_hand"
  Group = -> [Binder014,Sketch016,Pad001,Pocket012,Mirrored003,Binder015]
  Origin = -> Origin006
  Placement = pos=(0,-0.0522642,0.497261) rot=(1,0,0;0.10472rad)
  Tip = -> Mirrored003
  expr: Placement = placement(vector(0; 0; 0); rotation(0; 0; 6)) * placement(vector(0; 0; 0.5); rotation(0; 0; 0))
FEATURE [Part::Part2DObjectPython] Line002  # Draft 2D object (typed FeaturePython)
  Area = 0
  ChamferSize = 0
  Closed = false
  End = (-164.614,0,1)
  FilletRadius = 0
  Length = 329.23
  MakeFace = true
  Placement = pos=(0,0,-105) rot=(0.94131,-0.323415,-0.096634;0.894457rad)
  Points = (2) [(180.509,71.9679,18.9705),(-134.47,85.3935,113.84)]
  Start = (164.614,0,0)
  Subdivisions = 0
  expr: .End.x = -<<Line>>.Start.x
  expr: .End.y = <<Line>>.Start.y
  expr: .End.z = <<Line>>.Start.z + 1 mm
  expr: Start = <<Line>>.Start
FEATURE [Part::Part2DObjectPython] Line003  # Draft 2D object (typed FeaturePython)
  Area = 0
  ChamferSize = 0
  Closed = false
  End = (-290.084,134.058,15.8523)
  FilletRadius = 0
  Length = 184.214
  MakeFace = true
  Placement = pos=(0,0,0) rot=(0.94131,-0.323415,-0.096634;0.523599rad)
  Points = (2) [(-161.952,-0.764822,29.4927),(-295.231,123.319,1.6585)]
  Start = (-164.614,0,1)
  Subdivisions = 0
  expr: End = <<DatumPoint001>>.Placement.Base
  expr: Start = <<Line002>>.End
FEATURE [PartDesign::Point] DatumPoint
  AttacherType = Attacher::AttachEnginePoint
  MapMode = 40
  Placement = pos=(1e-16,1e-16,0.5) rot=(0,0,1;0rad)
  Support = -> [Z_Axis001,Line002]
FEATURE [PartDesign::Line] DatumLine
  AttacherType = Attacher::AttachEngineLine
  Length = 20
  MapMode = 29
  ResizeMode = 0
  Support = -> [Z_Axis001]
FEATURE [PartDesign::Plane] DatumPlane
  Length = 1124.49
  MapMode = 13
  Placement = pos=(96.6946,44.686,5.03002) rot=(-0.014044,0.998455,0.053755;3.1431rad)
  ResizeMode = 0
  Support = -> [Line,Line002]
  Width = 455.81
FEATURE [Sketcher::SketchObject] Sketch054
  ExternalGeometry = -> [Line002]
  FullyConstrained = true
  MapMode = 7
  Placement = pos=(164.614,-1.42e-14,0) rot=(0.880512,-0.347772,-0.322108;1.77331rad)
  Support = -> [Line]
  sketch-geometry (3):
    g0: LineSegment StartX=-2.68886 StartY=0.203704 StartZ=0 EndX=-3.624e-13 EndY=4.499e-13 EndZ=0
    g1: LineSegment StartX=-3.624e-13 StartY=4.499e-13 StartZ=0 EndX=1.3549e-12 EndY=2.69656 EndZ=0
    g2: ArcOfCircle CenterX=-2.5 CenterY=2.69656 CenterZ=0 NormalX=0 NormalY=0 NormalZ=1 AngleXU=0 Radius=2.5 StartAngle=4.63677 EndAngle=6.28319
  constraints (7):
    c: PointOnObject(g0,g-3)
    c: Coincident(g0,g-3)
    c: Coincident(g0,g1)
    c: PointOnObject(g1,g-2)
    c: Tangent(g2,g1) = -1.5708
    c: Tangent(g2,g0) = -1.5708
    c: Radius(g2) = 2.5
FEATURE [Sketcher::SketchObject] Sketch055
  ExternalGeometry = -> [Line]
  FullyConstrained = true
  MapMode = 7
  Placement = pos=(164.614,-3.55e-14,8.53e-14) rot=(0.577934,0.577934,0.576181;2.09615rad)
  Support = -> [Line002]
  sketch-geometry (3):
    g0: LineSegment StartX=-1.5028e-12 StartY=2.78439 StartZ=0 EndX=3.669e-13 EndY=2.616e-13 EndZ=0
    g1: LineSegment StartX=3.669e-13 StartY=2.616e-13 StartZ=0 EndX=2.76831 EndY=0.298829 EndZ=0
    g2: ArcOfCircle CenterX=2.5 CenterY=2.78439 CenterZ=0 NormalX=0 NormalY=0 NormalZ=1 AngleXU=0 Radius=2.5 StartAngle=3.14159 EndAngle=4.81992
  constraints (7):
    c: PointOnObject(g0,g-2)
    c: Coincident(g0,g-3)
    c: Coincident(g0,g1)
    c: PointOnObject(g1,g-3)
    c: Tangent(g2,g1) = -1.5708
    c: Tangent(g2,g0) = -1.5708
    c: Radius(g2) = 2.5
FEATURE [Sketcher::SketchObject] Sketch056
  ExternalGeometry = -> [Line002]
  FullyConstrained = true
  MapMode = 7
  Placement = pos=(-164.614,-1.42e-14,1) rot=(0.880889,0.347921,0.320915;1.77694rad)
  Support = -> [Line003]
  sketch-geometry (3):
    g0: LineSegment StartX=0 StartY=2.68463 StartZ=0 EndX=-5.68e-14 EndY=-5.68e-14 EndZ=0
    g1: LineSegment StartX=-5.68e-14 StartY=-5.68e-14 StartZ=0 EndX=2.67783 EndY=0.190965 EndZ=0
    g2: ArcOfCircle CenterX=2.5 CenterY=2.68463 CenterZ=0 NormalX=0 NormalY=0 NormalZ=1 AngleXU=0 Radius=2.5 StartAngle=3.14159 EndAngle=4.78358
  constraints (7):
    c: PointOnObject(g0,g-2)
    c: Coincident(g0,g-3)
    c: Coincident(g0,g1)
    c: PointOnObject(g1,g-3)
    c: Tangent(g2,g1) = -1.5708
    c: Tangent(g2,g0) = -1.5708
    c: Radius(g2) = 2.5
FEATURE [Sketcher::SketchObject] Sketch053  label="sink_pad_sketch"
  ExternalGeometry = -> [Line002,Line,Line003,Sketch056,Sketch054,Sketch055]
  FullyConstrained = true
  MapMode = 5
  Placement = pos=(96.6946,44.686,5.03002) rot=(0.967434,0.013608,0.252758;0.111187rad)
  Support = -> [DatumPlane]
  sketch-geometry (5):
    g0: LineSegment StartX=-380.445 StartY=100.694 StartZ=0 EndX=-261.308 EndY=-34.7826 EndZ=0
    g1: LineSegment StartX=-261.308 StartY=-34.7826 StartZ=0 EndX=65.6222 EndY=-44.0353 EndZ=0
    g2: LineSegment StartX=65.6222 StartY=-44.0353 StartZ=0 EndX=192.145 EndY=84.4891 EndZ=0
    g3: LineSegment StartX=192.145 StartY=84.4891 StartZ=0 EndX=-380.445 EndY=100.694 EndZ=0
    g4: LineSegment StartX=195.826 StartY=84.3849 StartZ=0 EndX=192.145 EndY=84.4891 EndZ=0
  constraints (18):
    c: Coincident(g0,g1)
    c: Coincident(g1,g2)
    c: Coincident(g2,g3)
    c: Coincident(g3,g0)
    c: Parallel(g0,g-5)
    c: Parallel(g1,g-3)
    c: Parallel(g1,g3)
    c: Parallel(g2,g-4)
    c: Coincident(g4,g-4)
    c: Coincident(g4,g2)
    c: Parallel(g4,g3)
    c: PointOnObject(g-8,g1)
    c: PointOnObject(g-7,g2)
    c: PointOnObject(g-6,g0)
    c: Distance(g2) = 180.351  'left'
    c: Distance(g1) = 327.061  'back'
    c: Distance(g3) = 572.82  'front'
    c: Distance(g0) = 180.41  'right'
FEATURE [PartDesign::FeaturePython] BaseBend001  label="sink_BaseBend"  # WARN: FeaturePython — macro-defined, semantics opaque (R4)
  BendSide = 0
  BendSketch = -> Sketch053
  MidPlane = false
  Reverse = false
  length = 1000
  radius = 2
  thickness = 0.5
FEATURE [Sketcher::SketchObject] Sketch050
  ExternalGeometry = -> [DatumLine,Sketch054]
  FullyConstrained = true
  MapMode = 7
  Placement = pos=(288.375,132.232,13.8981) rot=(0.259213,0.656292,0.708583;2.59582rad)
  Support = -> [Line,Sketch053]
  sketch-geometry (6):
    g0: ArcOfCircle CenterX=2.5 CenterY=2.69656 CenterZ=0 NormalX=0 NormalY=0 NormalZ=1 AngleXU=0 Radius=2.5 StartAngle=3.14159 EndAngle=4.788
    g1: LineSegment StartX=2.68886 StartY=0.203704 StartZ=0 EndX=2.65108 EndY=0.702276 EndZ=0
    g2: LineSegment StartX=-1.4784e-12 StartY=2.69656 StartZ=0 EndX=0 EndY=102.697 EndZ=0
    g3: LineSegment StartX=0 StartY=102.697 StartZ=0 EndX=0.5 EndY=102.697 EndZ=0
    g4: LineSegment StartX=0.5 StartY=102.697 StartZ=0 EndX=0.5 EndY=2.69656 EndZ=0
    g5: ArcOfCircle CenterX=2.5 CenterY=2.69656 CenterZ=0 NormalX=0 NormalY=0 NormalZ=1 AngleXU=0 Radius=2 StartAngle=3.14159 EndAngle=4.788
  constraints (15):
    c: PointOnObject(g2,g-2)
    c: Coincident(g2,g3)
    c: Horizontal(g3)
    c: Coincident(g3,g4)
    c: Vertical(g4)
    c: Coincident(g5,g0)
    c: Coincident(g5,g1)
    c: Perpendicular(g5,g1)
    c: Tangent(g5,g4) = -1.5708
    c: DistanceY(g4,g4) = 100
    c: Tangent(g2,g0) = 1.5708
    c: Coincident(g1,g0)
    c: Distance(g1) = 0.5
    c: Coincident(g0,g-4)
    c: Coincident(g0,g-4)
FEATURE [Sketcher::SketchObject] Sketch051
  ExternalGeometry = -> [Line]
  FullyConstrained = true
  MapMode = 7
  Placement = pos=(163.521,-4.09e-14,0.0033192) rot=(0.577934,0.577934,0.576181;2.09615rad)
  Support = -> [Line002,Sketch053]
  sketch-geometry (6):
    g0: ArcOfCircle CenterX=2.5 CenterY=2.78439 CenterZ=0 NormalX=0 NormalY=0 NormalZ=1 AngleXU=0 Radius=2.5 StartAngle=3.14159 EndAngle=4.81992
    g1: LineSegment StartX=0.5 StartY=2.78439 StartZ=0 EndX=0.5 EndY=102.784 EndZ=0
    g2: LineSegment StartX=0.5 StartY=102.784 StartZ=0 EndX=-2.7e-15 EndY=102.784 EndZ=0
    g3: LineSegment StartX=-2.7e-15 StartY=102.784 StartZ=0 EndX=-2.7e-15 EndY=2.78439 EndZ=0
    g4: ArcOfCircle CenterX=2.5 CenterY=2.78439 CenterZ=0 NormalX=0 NormalY=0 NormalZ=1 AngleXU=0 Radius=2 StartAngle=3.14159 EndAngle=4.81992
    g5: LineSegment StartX=2.76831 StartY=0.298829 StartZ=0 EndX=2.71465 EndY=0.795941 EndZ=0
  constraints (16):
    c: PointOnObject(g0,g-2)
    c: Coincident(g1,g2)
    c: PointOnObject(g2,g-2)
    c: Coincident(g2,g3)
    c: Perpendicular(g3,g2)
    c: Perpendicular(g2,g1)
    c: Tangent(g1,g4) = 1.5708
    c: Coincident(g4,g0)
    c: Radius(g4) = 2
    c: Tangent(g3,g0) = -1.5708
    c: DistanceY(g3,g3) = 100
    c: Coincident(g5,g0)
    c: Coincident(g5,g4)
    c: Tangent(g0,g-3) = -1.5708
    c: Perpendicular(g4,g5)
    c: Distance(g5) = 0.5
FEATURE [Sketcher::SketchObject] Sketch052
  ExternalGeometry = -> [Sketch056,DatumLine]
  FullyConstrained = true
  MapMode = 7
  Placement = pos=(-288.382,132.239,15.6508) rot=(0.880889,0.347921,0.320915;1.77694rad)
  Support = -> [Line003,Sketch053]
  sketch-geometry (6):
    g0: ArcOfCircle CenterX=2.5 CenterY=2.68463 CenterZ=0 NormalX=0 NormalY=0 NormalZ=1 AngleXU=0 Radius=2.5 StartAngle=3.14159 EndAngle=4.78358
    g1: LineSegment StartX=5.64e-14 StartY=2.68463 StartZ=0 EndX=7.79e-14 EndY=102.685 EndZ=0
    g2: LineSegment StartX=7.79e-14 StartY=102.685 StartZ=0 EndX=0.5 EndY=102.685 EndZ=0
    g3: LineSegment StartX=0.5 StartY=102.685 StartZ=0 EndX=0.5 EndY=2.68463 EndZ=0
    g4: ArcOfCircle CenterX=2.5 CenterY=2.68463 CenterZ=0 NormalX=0 NormalY=0 NormalZ=1 AngleXU=0 Radius=2 StartAngle=3.14159 EndAngle=4.78358
    g5: LineSegment StartX=2.67783 StartY=0.190965 StartZ=0 EndX=2.64227 EndY=0.689698 EndZ=0
  constraints (15):
    c: Coincident(g1,g2)
    c: Coincident(g2,g3)
    c: Tangent(g3,g4) = -1.5708
    c: Coincident(g4,g0)
    c: Perpendicular(g2,g1)
    c: Perpendicular(g3,g2)
    c: DistanceY(g1,g1) = 100
    c: Coincident(g5,g0)
    c: Coincident(g5,g4)
    c: Perpendicular(g4,g5)
    c: Coincident(g0,g-3)
    c: Parallel(g1,g-4)
    c: Tangent(g0,g1) = 1.5708
    c: Distance(g5) = 0.5
    c: Coincident(g0,g-3)
FEATURE [PartDesign::Pad] Pad013
  BaseFeature = -> BaseBend001
  Direction = (0.681109,-0.72773,-0.0806251)
  Length = 180.41
  Length2 = 10
  Profile = -> Sketch052
  ReferenceAxis = -> Sketch052 [N_Axis]
  Type = 0
  expr: Length = <<sink_pad_sketch>>.Constraints.right
FEATURE [PartDesign::Pad] Pad014
  BaseFeature = -> Pad013
  Direction = (0.68133,0.727966,0.0765123)
  Length = 180.351
  Length2 = 10
  Profile = -> Sketch050
  ReferenceAxis = -> Sketch050 [N_Axis]
  Reversed = true
  Type = 0
  expr: Length = <<sink_pad_sketch>>.Constraints.left
FEATURE [PartDesign::Pad] Pad015
  BaseFeature = -> Pad014
  Direction = (0.999995,1e-16,-0.00303739)
  Length = 327.061
  Length2 = 10
  Profile = -> Sketch051
  ReferenceAxis = -> Sketch051 [N_Axis]
  Reversed = true
  Type = 0
  expr: Length = <<sink_pad_sketch>>.Constraints.back
FEATURE [Sketcher::SketchObject] Sketch081
  ExternalGeometry = -> [Sketch053]
  FullyConstrained = false
  MapMode = 5
  Placement = pos=(96.6946,44.686,5.03002) rot=(-0.014044,0.998455,0.053755;3.1431rad)
  Support = -> [DatumPlane]
  sketch-geometry (2):
    g0: Circle CenterX=-104.279 CenterY=-83.2053 CenterZ=0 NormalX=0 NormalY=0 NormalZ=1 AngleXU=0 Radius=25.1105
    g1: Circle CenterX=216.965 CenterY=-71.8137 CenterZ=0 NormalX=0 NormalY=0 NormalZ=1 AngleXU=0 Radius=31.7244
FEATURE [Sketcher::SketchObject] Sketch008
  AttachmentOffset = pos=(0,0,0) rot=(0,1,0;1.5708rad)
  ExternalGeometry = -> [Sketch007,Sketch053,Sketch054]
  FullyConstrained = false
  MapMode = 7
  Placement = pos=(164.614,1.42e-14,0) rot=(0.852419,0.369717,0.369717;1.7298rad)
  Support = -> [Binder]
  sketch-geometry (17):
    g0: LineSegment StartX=175.907 StartY=87 StartZ=0 EndX=296.262 EndY=87 EndZ=0
    g1: LineSegment StartX=296.262 StartY=87 StartZ=0 EndX=296.262 EndY=16.5868 EndZ=0
    g2: LineSegment StartX=296.262 StartY=16.5868 StartZ=0 EndX=180.907 EndY=16.5868 EndZ=0
    g3: LineSegment StartX=-74 StartY=-1.883e-13 StartZ=0 EndX=-74 EndY=87 EndZ=0
    g4: LineSegment StartX=-74 StartY=87 StartZ=0 EndX=6 EndY=87 EndZ=0
    g5: LineSegment StartX=180.907 StartY=16.5868 StartZ=0 EndX=180.907 EndY=82 EndZ=0
    g6: ArcOfCircle CenterX=175.907 CenterY=82 CenterZ=0 NormalX=0 NormalY=0 NormalZ=1 AngleXU=0 Radius=5 StartAngle=-9e-16 EndAngle=1.5708
    g7: ArcOfCircle CenterX=6 CenterY=82 CenterZ=0 NormalX=0 NormalY=0 NormalZ=1 AngleXU=0 Radius=5 StartAngle=1.5708 EndAngle=3.14159
    g8: LineSegment StartX=0 StartY=0 StartZ=0 EndX=181.113 EndY=13.8981 EndZ=0
    g9: LineSegment StartX=181.113 StartY=13.8981 StartZ=0 EndX=180.907 EndY=16.5868 EndZ=0
    g10: LineSegment StartX=1 StartY=82 StartZ=0 EndX=1 EndY=21.4205 EndZ=0
    g11: LineSegment StartX=1 StartY=21.4205 StartZ=0 EndX=1 EndY=-1.883e-13 EndZ=0
    g12: ArcOfCircle CenterX=6 CenterY=21.4205 CenterZ=0 NormalX=0 NormalY=0 NormalZ=1 AngleXU=0 Radius=5 StartAngle=3.14159 EndAngle=4.18879
    g13: ArcOfCircle CenterX=1 CenterY=12.7602 CenterZ=0 NormalX=0 NormalY=0 NormalZ=1 AngleXU=0 Radius=5 StartAngle=1e-16 EndAngle=1.0472
    g14: LineSegment StartX=6 StartY=0 StartZ=0 EndX=6 EndY=12.7602 EndZ=0
    g15: LineSegment StartX=6 StartY=0 StartZ=0 EndX=1 EndY=-1.883e-13 EndZ=0
    g16: LineSegment StartX=1 StartY=-1.883e-13 StartZ=0 EndX=-74 EndY=-1.883e-13 EndZ=0
  constraints (46):
    c: Tangent(g7,g4) = 1.5708
    c: Coincident(g3,g4)
    c: Tangent(g6,g0) = 1.5708
    c: Coincident(g2,g5)
    c: Tangent(g5,g6) = -1.5708
    c: Coincident(g2,g1)
    c: Coincident(g1,g0)
    c: Coincident(g3,g16)
    c: Equal(g7,g6)
    c: Radius(g7) = 5
    c: PointOnObject(g4,g-3)
    c: PointOnObject(g3,g-3)
    c: PointOnObject(g0,g-3)
    c: PointOnObject(g0,g-3)
    c: Vertical(g5)
    c: DistanceX(g4,g4) = 80
    c: Vertical(g3)
    c: Horizontal(g2)
    c: Vertical(g1)
    c: Coincident(g-1,g8)
    c: Coincident(g8,g9)
    c: PointOnObject(g-4,g9)
    c: Perpendicular(g8,g9)
    c: Perpendicular(g-5,g8)
    c: Equal(g9,g-5)
    c: Coincident(g2,g9)
    c: PointOnObject(g15,g-1)
    c: Coincident(g10,g11)
    c: Vertical(g10)
    c: Vertical(g11)
    c: DistanceX(g11) = 1
    c: Coincident(g12,g10)
    c: PointOnObject(g13,g11)
    c: Coincident(g14,g15)
    c: Vertical(g14)
    c: Tangent(g14,g13) = -1.5708
    c: Tangent(g13,g12) = 1.5708
    c: Tangent(g12,g11)
    c: Radius(g13) = 5
    c: Equal(g13,g12)
    c: DistanceY(g10) = 21.4205
    c: Tangent(g7,g10) = -1.5708
    c: Coincident(g15,g16)
    c: Horizontal(g16)
    c: Coincident(g15,g11)
    c: PointOnObject(g11,g-1)
FEATURE [Sketcher::SketchObject] Sketch084
  ExternalGeometry = -> [Sketch053,Sketch050]
  FullyConstrained = true
  MapMode = 2
  Placement = pos=(164.614,1.42e-14,0) rot=(0.852419,0.369717,0.369717;1.7298rad)
  Support = -> [Sketch008]
  sketch-geometry (5):
    g0: LineSegment StartX=191.259 StartY=12.3808 StartZ=0 EndX=180.907 EndY=147.285 EndZ=0
    g1: LineSegment StartX=180.907 StartY=147.285 StartZ=0 EndX=180.907 EndY=16.5868 EndZ=0
    g2: LineSegment StartX=180.907 StartY=16.5868 StartZ=0 EndX=181.098 EndY=14.1012 EndZ=0
    g3: LineSegment StartX=181.288 StartY=11.6157 StartZ=0 EndX=191.259 EndY=12.3808 EndZ=0
    g4: LineSegment StartX=181.288 StartY=11.6157 StartZ=0 EndX=181.098 EndY=14.1012 EndZ=0
  constraints (13):
    c: Coincident(g1,g2)
    c: Vertical(g1)
    c: Coincident(g3,g0)
    c: Perpendicular(g2,g3)
    c: Distance(g0,g2) = 10
    c: Perpendicular(g3,g0)
    c: Coincident(g0,g1)
    c: Coincident(g4,g3)
    c: Coincident(g4,g2)
    c: Parallel(g4,g2)
    c: Coincident(g2,g-3)
    c: Equal(g4,g2)
    c: Coincident(g1,g-4)
FEATURE [Sketcher::SketchObject] Sketch085
  AttachmentOffset = pos=(0,0,0) rot=(0,1,0;1.5708rad)
  ExternalGeometry = -> [Sketch056,Sketch053,Sketch007]
  FullyConstrained = false
  MapMode = 7
  Placement = pos=(-164.614,-1.42e-14,0) rot=(-0.852419,0.369717,0.369717;4.55339rad)
  Support = -> [Binder]
  sketch-geometry (23):
    g0: LineSegment StartX=-181.123 StartY=15.6508 StartZ=0 EndX=-180.907 EndY=18.3267 EndZ=0
    g1: LineSegment StartX=-181.123 StartY=15.6508 StartZ=0 EndX=-2.84e-14 EndY=1 EndZ=0
    g2: LineSegment StartX=-180.907 StartY=18.3267 StartZ=0 EndX=-215.041 EndY=18.3267 EndZ=0
    g3: LineSegment StartX=-215.041 StartY=18.3267 StartZ=0 EndX=-215.041 EndY=87 EndZ=0
    g4: LineSegment StartX=-215.041 StartY=87 StartZ=0 EndX=-175.907 EndY=87 EndZ=0
    g5: LineSegment StartX=15.5786 StartY=0 StartZ=0 EndX=15.5786 EndY=87 EndZ=0
    g6: LineSegment StartX=15.5786 StartY=87 StartZ=0 EndX=-6 EndY=87 EndZ=0
    g7: LineSegment StartX=-180.907 StartY=82 StartZ=0 EndX=-180.907 EndY=18.3267 EndZ=0
    g8: ArcOfCircle CenterX=-175.907 CenterY=82 CenterZ=0 NormalX=0 NormalY=0 NormalZ=1 AngleXU=0 Radius=5 StartAngle=1.5708 EndAngle=3.14159
    g9: ArcOfCircle CenterX=-6 CenterY=82 CenterZ=0 NormalX=0 NormalY=0 NormalZ=1 AngleXU=0 Radius=5 StartAngle=4.00187e-11 EndAngle=1.5708
    g10: LineSegment StartX=-215.041 StartY=87 StartZ=0 EndX=-215.041 EndY=111.104 EndZ=0
    g11: LineSegment StartX=-215.041 StartY=111.104 StartZ=0 EndX=-174.64 EndY=111.104 EndZ=0
    g12: LineSegment StartX=-174.64 StartY=111.104 StartZ=0 EndX=-175.907 EndY=87 EndZ=0
    g13: LineSegment StartX=15.5786 StartY=87 StartZ=0 EndX=15.5786 EndY=112.942 EndZ=0
    g14: LineSegment StartX=15.5786 StartY=112.942 StartZ=0 EndX=-6 EndY=112.942 EndZ=0
    g15: LineSegment StartX=-6 StartY=112.942 StartZ=0 EndX=-6 EndY=87 EndZ=0
    g16: LineSegment StartX=-1 StartY=82 StartZ=0 EndX=-1 EndY=22.4417 EndZ=0
    g17: LineSegment StartX=-1 StartY=22.4417 StartZ=0 EndX=-1 EndY=0 EndZ=0
    g18: ArcOfCircle CenterX=-6 CenterY=22.4417 CenterZ=0 NormalX=0 NormalY=0 NormalZ=1 AngleXU=0 Radius=5 StartAngle=5.23599 EndAngle=6.28319
    g19: ArcOfCircle CenterX=-1 CenterY=13.7814 CenterZ=0 NormalX=0 NormalY=0 NormalZ=1 AngleXU=0 Radius=5 StartAngle=2.0944 EndAngle=3.14159
    g20: LineSegment StartX=-6 StartY=0 StartZ=0 EndX=-6 EndY=13.7814 EndZ=0
    g21: LineSegment StartX=-6 StartY=0 StartZ=0 EndX=-1 EndY=0 EndZ=0
    g22: LineSegment StartX=-1 StartY=0 StartZ=0 EndX=15.5786 EndY=0 EndZ=0
  constraints (58):
    c: PointOnObject(g-4,g0)
    c: Coincident(g1,g0)
    c: Coincident(g1,g-3)
    c: Parallel(g1,g-4)
    c: Parallel(g-3,g0)
    c: Equal(g-3,g0)
    c: Coincident(g2,g3)
    c: Coincident(g3,g4)
    c: Coincident(g7,g2)
    c: Horizontal(g2)
    c: Horizontal(g4)
    c: Vertical(g3)
    c: Coincident(g2,g0)
    c: Coincident(g22,g5)
    c: Coincident(g5,g6)
    c: Horizontal(g6)
    c: Vertical(g5)
    c: PointOnObject(g5,g-5)
    c: PointOnObject(g4,g-5)
    c: Vertical(g7)
    c: Tangent(g6,g9) = -1.5708
    c: Tangent(g8,g4) = 1.5708
    c: Tangent(g8,g7) = -1.5708
    c: Coincident(g9,g16) = 1.5708
    c: Equal(g9,g8)
    c: Radius(g9) = 5
    c: Coincident(g3,g10)
    c: Vertical(g10)
    c: Coincident(g10,g11)
    c: Horizontal(g11)
    c: Coincident(g11,g12)
    c: Coincident(g12,g8)
    c: Coincident(g5,g13)
    c: Vertical(g13)
    c: Coincident(g13,g14)
    c: Horizontal(g14)
    c: Coincident(g14,g15)
    c: Coincident(g15,g9)
    c: Vertical(g15)
    c: Coincident(g16,g17)
    c: Vertical(g16)
    c: Vertical(g17)
    c: DistanceX(g9) = -1
    c: PointOnObject(g21,g-1)
    c: Coincident(g18,g16)
    c: PointOnObject(g19,g17)
    c: Coincident(g20,g21)
    c: Vertical(g20)
    c: Equal(g19,g18)
    c: Radius(g19) = 5
    c: DistanceY(g16) = 22.4417
    c: Tangent(g18,g17)
    c: Tangent(g20,g19) = 1.5708
    c: Tangent(g19,g18) = 1.5708
    c: Coincident(g21,g22)
    c: Horizontal(g21)
    c: Horizontal(g22)
    c: Coincident(g21,g17)
FEATURE [Sketcher::SketchObject] Sketch086
  ExternalGeometry = -> [Sketch056,Sketch053]
  FullyConstrained = false
  MapMode = 2
  Placement = pos=(-164.614,-1.42e-14,0) rot=(0.852419,-0.369717,-0.369717;1.7298rad)
  Support = -> [Sketch085]
  sketch-geometry (5):
    g0: LineSegment StartX=-181.123 StartY=15.6508 StartZ=0 EndX=-197.283 EndY=16.9579 EndZ=0
    g1: LineSegment StartX=-197.283 StartY=16.9579 StartZ=0 EndX=-197.067 EndY=19.6338 EndZ=0
    g2: LineSegment StartX=-197.067 StartY=19.6338 StartZ=0 EndX=-180.907 EndY=18.3267 EndZ=0
    g3: LineSegment StartX=-180.907 StartY=18.3267 StartZ=0 EndX=-181.123 EndY=15.6508 EndZ=0
    g4: LineSegment StartX=-181.123 StartY=15.6508 StartZ=0 EndX=-2.84e-14 EndY=1 EndZ=0
  constraints (13):
    c: Coincident(g0,g1)
    c: Coincident(g1,g2)
    c: Coincident(g2,g3)
    c: Parallel(g0,g2)
    c: Parallel(g1,g3)
    c: Perpendicular(g1,g0)
    c: Equal(g3,g-3)
    c: Parallel(g-3,g3)
    c: Coincident(g0,g3)
    c: PointOnObject(g-4,g3)
    c: Coincident(g4,g0)
    c: Coincident(g4,g-3)
    c: Parallel(g4,g-4)
FEATURE [PartDesign::Line] DatumLine001
  AttacherType = Attacher::AttachEngineLine
  AttachmentOffset = pos=(-290.084,134.058,0) rot=(0,0,1;0rad)
  Length = 20
  MapMode = 29
  Placement = pos=(-290.084,134.058,0) rot=(0,0,1;0rad)
  ResizeMode = 0
  Support = -> [Z_Axis001]
  expr: .AttachmentOffset.Base.x = -Line.End.x
  expr: .AttachmentOffset.Base.y = Line.End.y
FEATURE [PartDesign::Point] DatumPoint001
  AttacherType = Attacher::AttachEnginePoint
  MapMode = 40
  Placement = pos=(-290.084,134.058,15.8523) rot=(0,0,1;0rad)
  Support = -> [DatumPlane,DatumLine001]
FEATURE [Sketcher::SketchObject] Sketch082
  FullyConstrained = false
  MapMode = 5
  Placement = pos=(2e-16,-4.1e-15,0.5) rot=(0.999598,0.028253,-0.002347;0.107573rad)
  Support = -> [Local_CS]
  sketch-geometry (5):
    g0: ArcOfCircle CenterX=5.18e-14 CenterY=5.77e-14 CenterZ=0 NormalX=0 NormalY=0 NormalZ=1 AngleXU=0 Radius=10 StartAngle=3.79682 EndAngle=6.15786
    g1: ArcOfCircle CenterX=5.18e-14 CenterY=5.77e-14 CenterZ=0 NormalX=0 NormalY=0 NormalZ=1 AngleXU=0 Radius=10 StartAngle=6.15786 EndAngle=9.55011
    g2: ArcOfCircle CenterX=-7.93725 CenterY=-1 CenterZ=0 NormalX=0 NormalY=0 NormalZ=1 AngleXU=0 Radius=2 StartAngle=3.26692 EndAngle=4.71239
    g3: ArcOfCircle CenterX=7.93725 CenterY=-1 CenterZ=0 NormalX=0 NormalY=0 NormalZ=1 AngleXU=0 Radius=2 StartAngle=4.71239 EndAngle=6.15786
    g4: LineSegment StartX=7.93725 StartY=-3 StartZ=0 EndX=-7.93725 EndY=-3 EndZ=0
  constraints (12):
    c: Coincident(g0,g-1)
    c: Coincident(g0,g1)
    c: Coincident(g0,g1)
    c: Diameter(g0) = 20
    c: Horizontal(g4)
    c: Tangent(g4,g2) = 1.5708
    c: Tangent(g1,g2) = -1.5708
    c: Tangent(g1,g3) = -1.5708
    c: Tangent(g4,g3) = 1.5708
    c: Equal(g2,g3)
    c: Radius(g2) = 2
    c: DistanceY(g2) = -3
FEATURE [Sketcher::SketchObject] Sketch089
  ExternalGeometry = -> [Sketch053,Sketch055,Sketch007]
  FullyConstrained = true
  MapMode = 5
  Placement = pos=(0,0,0) rot=(1,0,0;1.5708rad)
  Support = -> [XZ_Plane001]
  sketch-geometry (6):
    g0: LineSegment StartX=164.623 StartY=2.78438 StartZ=0 EndX=-163.53 EndY=3.78111 EndZ=0
    g1: LineSegment StartX=-163.53 StartY=3.78111 StartZ=0 EndX=-163.538 EndY=0.996732 EndZ=0
    g2: LineSegment StartX=-163.538 StartY=0.996732 StartZ=0 EndX=164.614 EndY=3.61e-13 EndZ=0
    g3: LineSegment StartX=-163.53 StartY=3.78111 StartZ=0 EndX=-163.53 EndY=87 EndZ=0
    g4: LineSegment StartX=-163.53 StartY=3.78111 StartZ=0 EndX=-163.277 EndY=87 EndZ=0
    g5: LineSegment StartX=-163.277 StartY=87 StartZ=0 EndX=-163.53 EndY=87 EndZ=0
  constraints (16):
    c: Coincident(g-4,g0)
    c: Coincident(g0,g1)
    c: Coincident(g1,g2)
    c: Coincident(g2,g-4)
    c: Perpendicular(g2,g-4)
    c: Perpendicular(g0,g-4)
    c: Perpendicular(g1,g2)
    c: PointOnObject(g-3,g1)
    c: Coincident(g3,g0)
    c: Vertical(g3)
    c: PointOnObject(g3,g-5)
    c: Coincident(g4,g3)
    c: PointOnObject(g4,g-5)
    c: Coincident(g5,g4)
    c: Coincident(g5,g3)
    c: Parallel(g4,g1)
FEATURE [PartDesign::Pad] Pad018
  BaseFeature = -> Pad015
  Direction = (0,-1,2e-16)
  Length = 0.5
  Length2 = 10
  Profile = -> Sketch089
  ReferenceAxis = -> Sketch089 [N_Axis]
  Reversed = true
  Type = 0
  expr: Length = <<sink_BaseBend>>.thickness
FEATURE [PartDesign::Pocket] Pocket054
  BaseFeature = -> Pad018
  Direction = (0,1,-2e-16)
  Length = 5
  Length2 = 5
  Midplane = true
  Profile = -> Sketch007
  ReferenceAxis = -> Sketch007 [N_Axis]
  Refine = true
  Type = 1
FEATURE [PartDesign::FeaturePython] CornerRelief  # WARN: FeaturePython — macro-defined, semantics opaque (R4)
  BaseFeature = -> Pocket054
  ReliefSketch = 0
  Size = 10
  SizeRatio = 1
  XOffset = 0
  YOffset = 0
  baseObject = -> Pocket054 [Edge8,Edge21]
  kfactor = 0.5
FEATURE [PartDesign::FeaturePython] CornerRelief001  # WARN: FeaturePython — macro-defined, semantics opaque (R4)
  BaseFeature = -> CornerRelief
  ReliefSketch = 0
  Size = 10
  SizeRatio = 1
  XOffset = 0
  YOffset = 0
  baseObject = -> CornerRelief [Edge31,Edge32]
  kfactor = 0.5
  expr: Size = CornerRelief.Size
  expr: SizeRatio = CornerRelief.SizeRatio
FEATURE [PartDesign::FeaturePython] SketchOnSheet  # WARN: FeaturePython — macro-defined, semantics opaque (R4)
  BaseFeature = -> CornerRelief001
  Sketch = -> Sketch082
  baseObject = -> CornerRelief001 [Face13]
  kfactor = 0.5
FEATURE [PartDesign::Pad] Pad016
  BaseFeature = -> SketchOnSheet
  Direction = (0.68133,0.727966,0.0765123)
  Length = 10
  Length2 = 10
  Profile = -> Sketch050
  ReferenceAxis = -> Sketch050 [N_Axis]
  Type = 4
FEATURE [PartDesign::Pad] Pad017
  BaseFeature = -> Pad016
  Direction = (0.681109,-0.72773,-0.0806251)
  Length = 10
  Length2 = 10
  Profile = -> Sketch052
  ReferenceAxis = -> Sketch052 [N_Axis]
  Reversed = true
  Type = 0
FEATURE [PartDesign::Pocket] Pocket055
  BaseFeature = -> Pad017
  Direction = (-0.730107,0.683333,-2e-16)
  Length = 5
  Length2 = 5
  Profile = -> Sketch084
  ReferenceAxis = -> Sketch084 [N_Axis]
  Type = 0
FEATURE [PartDesign::Pocket] Pocket056
  BaseFeature = -> Pocket055
  Direction = (-0.730107,0.683333,-1e-16)
  Length = 5
  Length2 = 5
  Profile = -> Sketch008
  ReferenceAxis = -> Sketch008 [N_Axis]
  Type = 2
FEATURE [PartDesign::Body] Body001  label="sink_material_0.30ansi"
  Group = -> [Sketch001,BaseBend001,Sketch054,Sketch055,Sketch056,Pad013,Pad014,Pad015,Sketch004,Line,Binder,Sketch006,Line002,Line003,Sketch007,Sketch008,DatumPoint,Sketch050,DatumLine,DatumPlane,Sketch051,Sketch052,Sketch053,Sketch081,DatumLine001,DatumPoint001,Sketch089,Pad018,Pocket054,CornerRelief,CornerRelief001,Sketch082,SketchOnSheet,Pad016,Pad017,Sketch084,Pocket055,Pocket056,Sketch085,Sketch086,+14 more]
  Origin = -> Origin001
  Tip = -> Mirrored
